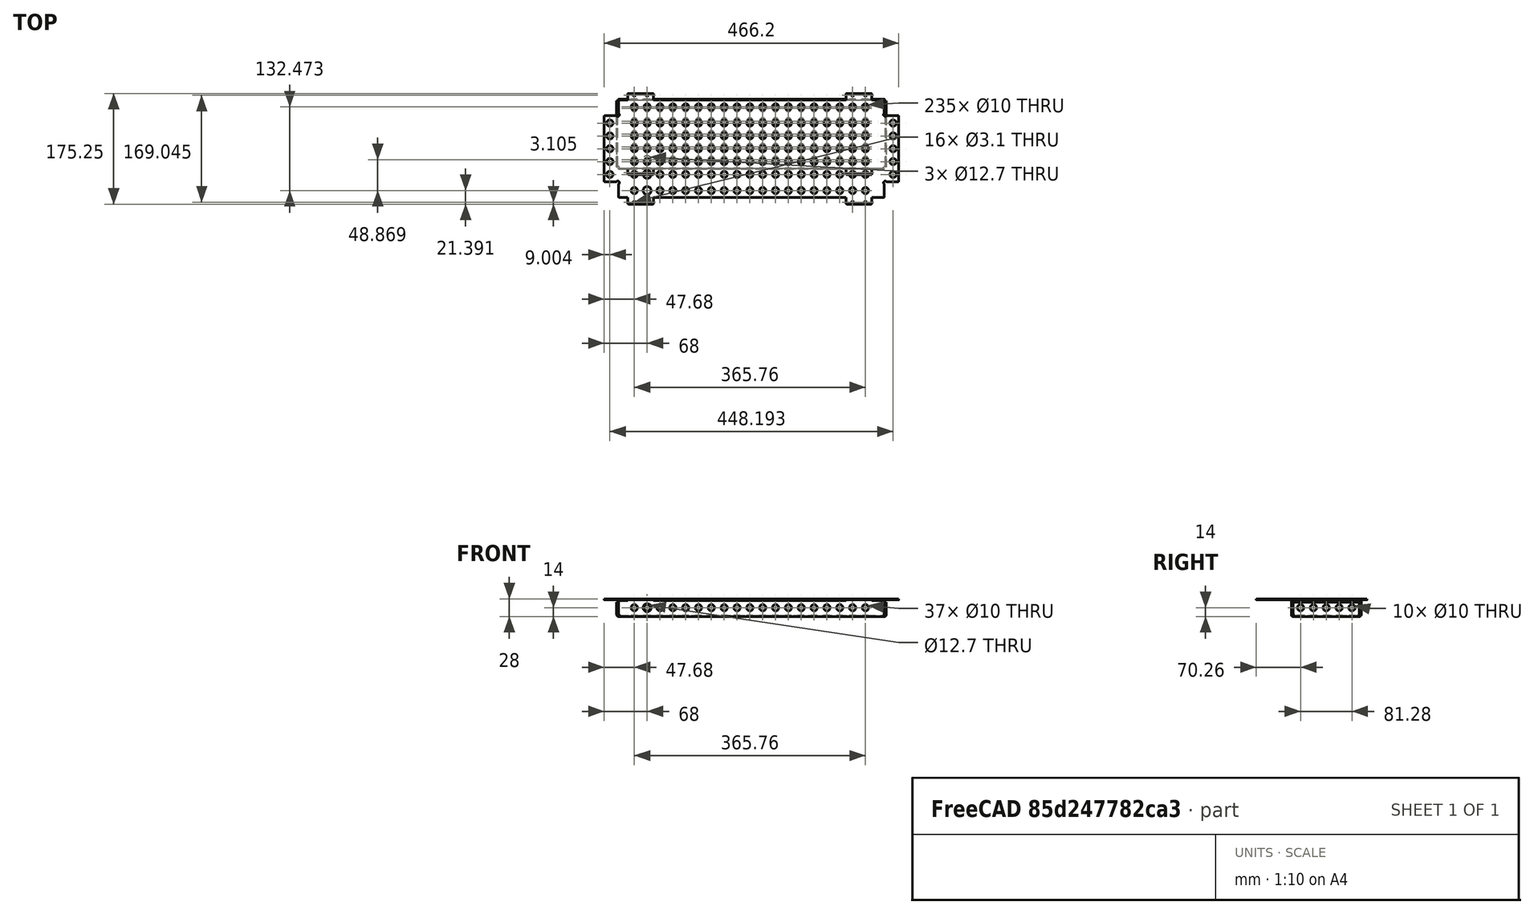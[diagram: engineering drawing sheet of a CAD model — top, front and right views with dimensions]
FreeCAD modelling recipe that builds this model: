
FCSTD DOCUMENT  (FreeCAD 0.21R33771 (Git))
Label: sheet_metal_rear_cover
License: All rights reserved
LicenseURL: http://en.wikipedia.org/wiki/All_rights_reserved
objects: TechDraw::DrawViewDimension×34, TechDraw::DrawViewBalloon×9, Sketcher::SketchObject×8, PartDesign::FeaturePython×7, PartDesign::Pocket×7, TechDraw::DrawViewAnnotation×6, PartDesign::LinearPattern×5, TechDraw::DrawSVGTemplate×5, TechDraw::DrawPage×5, PartDesign::MultiTransform×4, TechDraw::DrawViewPart×4, TechDraw::DrawProjGroupItem×4, PartDesign::Mirrored×2, Spreadsheet::Sheet×1, PartDesign::Plane×1, PartDesign::Fillet×1, PartDesign::Body×1, TechDraw::DrawViewSection×1, TechDraw::DrawProjGroup×1, Part::Feature×1
note: 108 computed .brp shape members not serialized (recipe doc carries the construction recipe); baked Part::Feature solids carry a one-line shape summary decoded from their .brp

FEATURE [PartDesign::FeaturePython] BaseShape  # WARN: FeaturePython — macro-defined, semantics opaque (R4)
  fillGaps = true
  flangeWidth = 5
  height = 25
  length = 420.42
  radius = 1.5
  shapeType = 1
  thickness = 1.5
  width = 110.7
  expr: height = Spreadsheet.h_cover - Spreadsheet.r_bending - Spreadsheet.t_cover
  expr: length = Spreadsheet.l_pcb - 2 * (Spreadsheet.r_bending + Spreadsheet.t_cover)
  expr: radius = Spreadsheet.r_bending
  expr: thickness = Spreadsheet.t_cover
  expr: width = Spreadsheet.h_pcb - 2 * Spreadsheet.d_ears + 2 * Spreadsheet.r_bending
FEATURE [PartDesign::FeaturePython] Bend  # WARN: FeaturePython — macro-defined, semantics opaque (R4)
  AutoMiter = true
  BaseFeature = -> BaseShape
  BendType = 0
  LengthList = [7.5]
  LengthSpec = 0
  ReliefFactor = 0.7
  UseReliefFactor = false
  angle = 90
  baseObject = -> BaseShape [Face21,Face3]
  bendAList = [90]
  extend1 = 0
  extend2 = 0
  gap1 = 0
  gap2 = 0
  invert = true
  kfactor = 0.5
  length = 7.5
  maxExtendDist = 5
  minGap = 0.2
  minReliefGap = 1
  miterangle1 = 0
  miterangle2 = 0
  offset = 0
  radius = 1.5
  reliefType = 0
  reliefd = 1
  reliefw = 0.8
  sketchflip = false
  sketchinvert = false
  unfold = false
  expr: length = Spreadsheet.d_ears - (Spreadsheet.t_cover + Spreadsheet.r_bending)
  expr: radius = Spreadsheet.r_bending
FEATURE [PartDesign::FeaturePython] Bend002  label="Bend001"  # WARN: FeaturePython — macro-defined, semantics opaque (R4)
  AutoMiter = true
  BaseFeature = -> Bend
  BendType = 0
  LengthList = [20]
  LengthSpec = 0
  ReliefFactor = 0.7
  UseReliefFactor = false
  angle = 90
  baseObject = -> Bend [Face17,Face22]
  bendAList = [90]
  extend1 = 0
  extend2 = 0
  gap1 = 0
  gap2 = 0
  invert = false
  kfactor = 0.5
  length = 20
  maxExtendDist = 5
  minGap = 0.2
  minReliefGap = 1
  miterangle1 = 0
  miterangle2 = 0
  offset = 0
  radius = 1.5
  reliefType = 0
  reliefd = 1
  reliefw = 0.8
  sketchflip = false
  sketchinvert = false
  unfold = false
  expr: radius = Spreadsheet.r_bending
FEATURE [Spreadsheet::Sheet] Spreadsheet
  cells = A1='y_first_screw; B1(y_first_screw)==3.1 mm; A2='x_first_screw; B2(x_first_screw)==7.47 mm; A3='dia_venting_hole; B3(dia_venting_hole)==10 mm; A4='h_pcb; B4(h_pcb)==128.7 mm; A5='h_cover; B5(h_cover)==28 mm; A6='t_cover; B6(t_cover)==1.5 mm; A7='d_ears; B7(d_ears)==10.5 mm; A8='d_venting_hole; B8(d_venting_hole)==4 * 5.08 mm; A9='l_pcb; B9(l_pcb)==426.42 mm; A10='d_grommet; B10(d_grommet)==25.4 mm / 2; A11='d_screws; B11(d_screws)==20 * 5.08 mm; A12='d_mounting_holes; B12(d_mounting_holes)==4 * 5.08 mm; A13='r_bending; B13(r_bending)==1.5 mm; A14='courtyard_edge; B14(courtyard_edge)==3 * t_cover; A15='dia_mounting_hole; B15(dia_mounting_hole)==3.1 mm; C15='Loose fit
FEATURE [Sketcher::SketchObject] Sketch001
  FullyConstrained = true
  MapMode = 5
  Placement = pos=(0,3.1e-15,28) rot=(0,0,1;0rad)
  expr: Constraints[0] = Spreadsheet.dia_mounting_hole
  expr: Constraints[1] = Spreadsheet.x_first_screw - Spreadsheet.r_bending - Spreadsheet.t_cover + Spreadsheet.d_mounting_holes
  expr: Constraints[2] = Spreadsheet.d_ears + Spreadsheet.r_bending - Spreadsheet.y_first_screw
  sketch-geometry (1):
    g0: Circle CenterX=24.79 CenterY=-8.9 CenterZ=0 NormalX=0 NormalY=0 NormalZ=1 AngleXU=0 Radius=1.55
  constraints (3):
    c: Diameter(g0) = 3.1
    c: DistanceX(g-1,g0) = 24.79
    c: DistanceY(g0,g-1) = 8.9
FEATURE [PartDesign::Pocket] Pocket001
  BaseFeature = -> Bend002
  Direction = (0,0,-1)
  Length = 1.6
  Length2 = 5
  Profile = -> Sketch001
  ReferenceAxis = -> Sketch001 [N_Axis]
  Type = 2
FEATURE [Sketcher::SketchObject] Sketch002
  ExternalGeometry = -> [Pocket001]
  FullyConstrained = true
  MapMode = 5
  Placement = pos=(0,-3,0) rot=(1,0,0;1.5708rad)
  Support = -> [Pocket001]
  expr: .Constraints.x_venting_hole = Spreadsheet.x_first_screw - Spreadsheet.r_bending - Spreadsheet.t_cover + Spreadsheet.d_venting_hole
  expr: .Constraints.y_venting_hole = (Spreadsheet.h_cover - 2 * Spreadsheet.t_cover - 2 * Spreadsheet.r_bending - 2 * Spreadsheet.courtyard_edge - Spreadsheet.dia_venting_hole) % Spreadsheet.d_venting_hole / 2 + Spreadsheet.t_cover + Spreadsheet.r_bending + Spreadsheet.courtyard_edge + Spreadsheet.dia_venting_hole / 2
  expr: Constraints[0] = Spreadsheet.dia_venting_hole
  sketch-geometry (1):
    g0: Circle CenterX=24.79 CenterY=14 CenterZ=0 NormalX=0 NormalY=0 NormalZ=1 AngleXU=0 Radius=5
  constraints (3):
    c: Diameter(g0) = 10
    c: DistanceY(g-1,g0) = 14  'y_venting_hole'
    c: DistanceX(g-1,g0) = 24.79  'x_venting_hole'
FEATURE [PartDesign::Pocket] Pocket002
  BaseFeature = -> Pocket001
  Direction = (0,1,-2e-16)
  Length = 1.6
  Length2 = 5
  Profile = -> Sketch002
  ReferenceAxis = -> Sketch002 [N_Axis]
  Type = 1
FEATURE [Sketcher::SketchObject] Sketch003
  FullyConstrained = true
  MapMode = 5
  Placement = pos=(0,0,0) rot=(1,0,0;3.14159rad)
  Support = -> [Pocket002]
  expr: .Constraints.x_venting_hole = Sketch002.Constraints.x_venting_hole
  expr: .Constraints.y_venting_hole = (Spreadsheet.h_pcb - trunc((Spreadsheet.h_pcb - 2 * (Spreadsheet.d_ears + Spreadsheet.r_bending + Spreadsheet.courtyard_edge) - Spreadsheet.dia_venting_hole) / Spreadsheet.d_venting_hole) * Spreadsheet.d_venting_hole) / 2 - Spreadsheet.d_ears - Spreadsheet.r_bending
  expr: Constraints[0] = Spreadsheet.dia_venting_hole
  sketch-geometry (1):
    g0: Circle CenterX=24.79 CenterY=-11.71 CenterZ=0 NormalX=0 NormalY=0 NormalZ=1 AngleXU=0 Radius=5
  constraints (3):
    c: Diameter(g0) = 10
    c: DistanceX(g-1,g0) = 24.79  'x_venting_hole'
    c: DistanceY(g0,g-1) = 11.71  'y_venting_hole'
FEATURE [PartDesign::Pocket] Pocket003
  BaseFeature = -> Pocket002
  Direction = (0,0,1)
  Length = 1.6
  Length2 = 5
  Profile = -> Sketch003
  ReferenceAxis = -> Sketch003 [N_Axis]
  Type = 0
FEATURE [Sketcher::SketchObject] Sketch004
  FullyConstrained = true
  MapMode = 5
  Placement = pos=(0,0,0) rot=(1,0,0;3.14159rad)
  Support = -> [Pocket003]
  expr: .Constraints.x_cable_feedthrough = Sketch003.Constraints.x_venting_hole + Spreadsheet.d_venting_hole
  expr: .Constraints.y_cable_feedthrough = Sketch003.Constraints.y_venting_hole
  expr: Constraints[0] = Spreadsheet.d_grommet
  sketch-geometry (1):
    g0: Circle CenterX=45.11 CenterY=-11.71 CenterZ=0 NormalX=0 NormalY=0 NormalZ=1 AngleXU=0 Radius=6.35
  constraints (3):
    c: Diameter(g0) = 12.7
    c: DistanceX(g-1,g0) = 45.11  'x_cable_feedthrough'
    c: DistanceY(g0,g-1) = 11.71  'y_cable_feedthrough'
FEATURE [PartDesign::LinearPattern] LinearPattern001
  Direction = -> Sketch002 [H_Axis]
  Length = 365.76
  Occurrences = 19
  expr: Length = trunc((Spreadsheet.l_pcb - (Sketch002.Constraints.x_venting_hole + 2 * Spreadsheet.r_bending + 2 * Spreadsheet.t_cover + Spreadsheet.courtyard_edge)) / Spreadsheet.d_venting_hole - 1) * Spreadsheet.d_venting_hole
  expr: Occurrences = trunc((Spreadsheet.l_pcb - (Sketch002.Constraints.x_venting_hole + Spreadsheet.r_bending + Spreadsheet.t_cover + Spreadsheet.courtyard_edge)) / Spreadsheet.d_venting_hole)
FEATURE [PartDesign::LinearPattern] LinearPattern002
  Direction = -> Sketch003 [V_Axis]
  Length = 81.28
  Occurrences = 5
  Reversed = true
  expr: Length = trunc((Spreadsheet.h_pcb - 2 * (Spreadsheet.d_ears + Spreadsheet.r_bending + Spreadsheet.courtyard_edge)) / Spreadsheet.d_venting_hole) * Spreadsheet.d_venting_hole
  expr: Occurrences = trunc((Spreadsheet.h_pcb - 2 * (Spreadsheet.d_ears + Spreadsheet.r_bending + Spreadsheet.courtyard_edge)) / Spreadsheet.d_venting_hole) + 1
FEATURE [PartDesign::LinearPattern] LinearPattern003
  Direction = -> Sketch003 [H_Axis]
  Length = 365.76
  Occurrences = 19
  expr: Length = trunc((Spreadsheet.l_pcb - (Sketch002.Constraints.x_venting_hole + 2 * Spreadsheet.r_bending + 2 * Spreadsheet.t_cover + Spreadsheet.courtyard_edge)) / Spreadsheet.d_venting_hole - 1) * Spreadsheet.d_venting_hole
  expr: Occurrences = trunc((Spreadsheet.l_pcb - (Sketch002.Constraints.x_venting_hole + 2 * Spreadsheet.r_bending + 2 * Spreadsheet.t_cover + Spreadsheet.courtyard_edge)) / Spreadsheet.d_venting_hole)
FEATURE [Sketcher::SketchObject] Sketch009
  FullyConstrained = true
  MapMode = 5
  Placement = pos=(-3,0,0) rot=(0.57735,-0.57735,-0.57735;2.0944rad)
  Support = -> [Pocket003]
  expr: Constraints[0] = Spreadsheet.dia_venting_hole
  expr: Constraints[1] = Sketch002.Constraints.y_venting_hole
  expr: Constraints[2] = Sketch003.Constraints.y_venting_hole
  sketch-geometry (1):
    g0: Circle CenterX=-11.71 CenterY=14 CenterZ=0 NormalX=0 NormalY=0 NormalZ=1 AngleXU=0 Radius=5
  constraints (3):
    c: Diameter(g0) = 10
    c: DistanceY(g-1,g0) = 14
    c: DistanceX(g0,g-1) = 11.71
FEATURE [PartDesign::Pocket] Pocket006
  BaseFeature = -> Pocket003
  Direction = (1,0,0)
  Length = 5
  Length2 = 5
  Profile = -> Sketch009
  ReferenceAxis = -> Sketch009 [N_Axis]
  Type = 1
FEATURE [PartDesign::Pocket] Pocket004
  BaseFeature = -> Pocket006
  Direction = (0,0,1)
  Length = 1.5
  Length2 = 5
  Profile = -> Sketch004
  ReferenceAxis = -> Sketch004 [N_Axis]
  Type = 0
FEATURE [Sketcher::SketchObject] Sketch005
  FullyConstrained = true
  MapMode = 5
  Placement = pos=(0,-3,0) rot=(1,0,0;1.5708rad)
  Support = -> [Pocket004]
  expr: .Constraints.x_cable_feedthrough = Sketch004.Constraints.x_cable_feedthrough
  expr: .Constraints.y_cable_feedthrough = Sketch002.Constraints.y_venting_hole
  expr: Constraints[0] = Spreadsheet.d_grommet
  sketch-geometry (1):
    g0: Circle CenterX=45.11 CenterY=14 CenterZ=0 NormalX=0 NormalY=0 NormalZ=1 AngleXU=0 Radius=6.35
  constraints (3):
    c: Diameter(g0) = 12.7
    c: DistanceY(g-1,g0) = 14  'y_cable_feedthrough'
    c: DistanceX(g-1,g0) = 45.11  'x_cable_feedthrough'
FEATURE [PartDesign::Pocket] Pocket005
  BaseFeature = -> Pocket004
  Direction = (0,1,-2e-16)
  Length = 1.6
  Length2 = 5
  Profile = -> Sketch005
  ReferenceAxis = -> Sketch005 [N_Axis]
  Type = 0
FEATURE [PartDesign::LinearPattern] LinearPattern005
  Direction = -> Sketch009 [H_Axis]
  Length = 81.28
  Occurrences = 5
  Reversed = true
  expr: Length = trunc((Spreadsheet.h_pcb - 2 * (Spreadsheet.d_ears + Spreadsheet.r_bending + Spreadsheet.courtyard_edge)) / Spreadsheet.d_venting_hole) * Spreadsheet.d_venting_hole
  expr: Occurrences = trunc((Spreadsheet.h_pcb - 2 * (Spreadsheet.d_ears + Spreadsheet.r_bending + Spreadsheet.courtyard_edge)) / Spreadsheet.d_venting_hole) + 1
FEATURE [PartDesign::Plane] DatumPlane
  AttachmentOffset = pos=(0,0,52.35) rot=(0,0,1;0rad)
  Length = 60
  MapMode = 5
  Placement = pos=(0,52.35,1.16e-14) rot=(0,0.707107,0.707107;3.14159rad)
  ResizeMode = 0
  Support = -> [XZ_Plane]
  Width = 60
  expr: .AttachmentOffset.Base.z = (Spreadsheet.h_pcb - 2 * Spreadsheet.d_ears - 2 * Spreadsheet.r_bending) / 2
FEATURE [PartDesign::MultiTransform] MultiTransform
  BaseFeature = -> Pocket005
  Originals = -> [Pocket002]
  Transformations = -> [LinearPattern001]
FEATURE [PartDesign::MultiTransform] MultiTransform001
  BaseFeature = -> MultiTransform
  Originals = -> [Pocket003]
  Transformations = -> [LinearPattern002,LinearPattern003]
FEATURE [PartDesign::MultiTransform] MultiTransform002
  BaseFeature = -> MultiTransform001
  Originals = -> [Pocket006]
  Transformations = -> [LinearPattern005]
FEATURE [Sketcher::SketchObject] Sketch010
  FullyConstrained = true
  MapMode = 5
  Placement = pos=(0,0,28) rot=(0,0,1;0rad)
  Support = -> [MultiTransform002]
  expr: Constraints[10] = Spreadsheet.d_ears
  expr: Constraints[11] = Spreadsheet.x_first_screw - (Spreadsheet.r_bending + Spreadsheet.t_cover) + 0.5 * Spreadsheet.d_venting_hole
  expr: Constraints[22] = 2 * Spreadsheet.d_mounting_holes
  expr: Constraints[33] = 2 * Spreadsheet.d_venting_hole
  expr: Constraints[34] = Spreadsheet.l_pcb - 2 * (Spreadsheet.t_cover + Spreadsheet.r_bending)
  expr: Constraints[35] = trunc((Spreadsheet.l_pcb - Spreadsheet.x_first_screw - 2 * Spreadsheet.t_cover - 2 * Spreadsheet.r_bending) / Spreadsheet.d_mounting_holes - 1) * Spreadsheet.d_mounting_holes + Spreadsheet.x_first_screw - Spreadsheet.r_bending - Spreadsheet.t_cover + 0.5 * Spreadsheet.d_venting_hole
  expr: Constraints[9] = Spreadsheet.t_cover
  sketch-geometry (12):
    g0: LineSegment StartX=0 StartY=-1.5 StartZ=0 EndX=14.63 EndY=-1.5 EndZ=0
    g1: LineSegment StartX=14.63 StartY=-1.5 StartZ=0 EndX=14.63 EndY=-12 EndZ=0
    g2: LineSegment StartX=14.63 StartY=-12 StartZ=0 EndX=0 EndY=-12 EndZ=0
    g3: LineSegment StartX=0 StartY=-12 StartZ=0 EndX=0 EndY=-1.5 EndZ=0
    g4: LineSegment StartX=55.27 StartY=-1.5 StartZ=0 EndX=360.07 EndY=-1.5 EndZ=0
    g5: LineSegment StartX=360.07 StartY=-1.5 StartZ=0 EndX=360.07 EndY=-12 EndZ=0
    g6: LineSegment StartX=360.07 StartY=-12 StartZ=0 EndX=55.27 EndY=-12 EndZ=0
    g7: LineSegment StartX=55.27 StartY=-12 StartZ=0 EndX=55.27 EndY=-1.5 EndZ=0
    g8: LineSegment StartX=400.71 StartY=-1.5 StartZ=0 EndX=420.42 EndY=-1.5 EndZ=0
    g9: LineSegment StartX=420.42 StartY=-1.5 StartZ=0 EndX=420.42 EndY=-12 EndZ=0
    g10: LineSegment StartX=420.42 StartY=-12 StartZ=0 EndX=400.71 EndY=-12 EndZ=0
    g11: LineSegment StartX=400.71 StartY=-12 StartZ=0 EndX=400.71 EndY=-1.5 EndZ=0
  constraints (36):
    c: Coincident(g0,g1)
    c: Coincident(g1,g2)
    c: Coincident(g2,g3)
    c: Coincident(g3,g0)
    c: Horizontal(g0)
    c: Horizontal(g2)
    c: Vertical(g1)
    c: Vertical(g3)
    c: PointOnObject(g0,g-2)
    c: DistanceY(g0,g-1) = 1.5
    c: DistanceY(g3,g3) = 10.5
    c: DistanceX(g2,g2) = 14.63
    c: Coincident(g4,g5)
    c: Coincident(g5,g6)
    c: Coincident(g6,g7)
    c: Coincident(g7,g4)
    c: Horizontal(g4)
    c: Horizontal(g6)
    c: Vertical(g5)
    c: Vertical(g7)
    c: Horizontal(g1,g6)
    c: Horizontal(g4,g0)
    c: DistanceX(g1,g6) = 40.64
    c: Coincident(g8,g9)
    c: Coincident(g9,g10)
    c: Coincident(g10,g11)
    c: Coincident(g11,g8)
    c: Horizontal(g8)
    c: Horizontal(g10)
    c: Vertical(g9)
    c: Vertical(g11)
    c: Horizontal(g8,g4)
    c: Horizontal(g10,g5)
    c: DistanceX(g5,g10) = 40.64
    c: DistanceX(g-1,g9) = 420.42
    c: DistanceX(g-1,g10) = 400.71
FEATURE [PartDesign::LinearPattern] LinearPattern
  Direction = -> Sketch010 [H_Axis]
  Length = 406.4
  Occurrences = 21
  expr: Length = trunc((Spreadsheet.l_pcb - (Spreadsheet.x_first_screw + Spreadsheet.r_bending + Spreadsheet.t_cover)) / Spreadsheet.d_mounting_holes) * Spreadsheet.d_mounting_holes
  expr: Occurrences = trunc((Spreadsheet.l_pcb - (Spreadsheet.x_first_screw + Spreadsheet.r_bending + Spreadsheet.t_cover)) / Spreadsheet.d_mounting_holes) + 1
FEATURE [PartDesign::Mirrored] Mirrored
  MirrorPlane = -> DatumPlane
FEATURE [PartDesign::MultiTransform] MultiTransform003
  BaseFeature = -> MultiTransform002
  Originals = -> [Pocket001]
  Transformations = -> [LinearPattern,Mirrored]
FEATURE [PartDesign::Pocket] Pocket007
  BaseFeature = -> MultiTransform003
  Direction = (0,0,-1)
  Length = 3
  Length2 = 5
  Profile = -> Sketch010
  ReferenceAxis = -> Sketch010 [N_Axis]
  Type = 0
  expr: Length = Spreadsheet.r_bending + Spreadsheet.t_cover
FEATURE [PartDesign::Mirrored] Mirrored001
  BaseFeature = -> Pocket007
  MirrorPlane = -> DatumPlane
  Originals = -> [Pocket007]
FEATURE [PartDesign::Fillet] Fillet
  Base = -> Mirrored001 [Edge562,Edge558,Edge476,Edge516,Edge515,Edge522,Edge582,Edge589,Edge591,Edge580,Edge403,Edge8,Edge2,Edge239,Edge513,Edge567]
  BaseFeature = -> Mirrored001
  Radius = 1
  SupportTransform = false
  UseAllEdges = false
FEATURE [PartDesign::FeaturePython] CornerRelief  # WARN: FeaturePython — macro-defined, semantics opaque (R4)
  BaseFeature = -> Fillet
  ReliefSketch = 0
  Size = 3
  SizeRatio = 1.5
  XOffset = 0
  YOffset = 0
  baseObject = -> Fillet [Edge45,Edge46]
  kfactor = 0.45
FEATURE [PartDesign::FeaturePython] CornerRelief001  # WARN: FeaturePython — macro-defined, semantics opaque (R4)
  BaseFeature = -> CornerRelief
  ReliefSketch = 0
  Size = 3
  SizeRatio = 1.5
  XOffset = 0
  YOffset = 0
  baseObject = -> CornerRelief [Edge46,Edge45]
  kfactor = 0.45
FEATURE [TechDraw::DrawSVGTemplate] Template
  EditableTexts = AUTHOR_NAME=P. Baus/J. Götzinger; DN=DN; DRAWING_TITLE=Backplane cover; FC-DATE=07/01/2034; FC-REV=1.0.0; FC-SC=1:2; FC-SH=1 / 5; FC-SI=A4; FreeCAD_DRAWING=TUD, Institut für Angewandte Physik, APQ; PN=PN; SI-1=Email: <email>; SI-3=Material: Stainless steel 430
  Height = 210
  Orientation = 1
  Template = <path>
  Width = 297
FEATURE [TechDraw::DrawSVGTemplate] Template001
  EditableTexts = AUTHOR_NAME=P. Baus/J. Götzinger; DN=DN; DRAWING_TITLE=Backplane cover; FC-DATE=07/01/2024; FC-REV=1.0.0; FC-SC=1:4; FC-SH=2 / 5; FC-SI=A4; FreeCAD_DRAWING=TUD, Institut für Angewandte Physik, APQ; PN=PN; SI-1=Email: <email>; SI-3=Material: Stainless steel 430
  Height = 210
  Orientation = 1
  Template = <path>
  Width = 297
FEATURE [TechDraw::DrawViewAnnotation] Annotation
  Font = osifont
  LineSpace = 100
  LockPosition = false
  MaxWidth = -1
  Rotation = 0
  Scale = 0.25
  ScaleType = 0
  Text = Bending sequence: Bend the central part first to maintain | tight tolerances in the horizontal direction.
  TextSize = 2.5
  TextStyle = 0
  X = 172.812
  Y = 74.2756
FEATURE [TechDraw::DrawSVGTemplate] Template002
  EditableTexts = AUTHOR_NAME=P. Baus/J. Götzinger; DN=DN; DRAWING_TITLE=Backplane cover; FC-DATE=07/01/2024; FC-REV=1.0.0; FC-SC=1:2; FC-SH=3 / 5; FC-SI=A4; FreeCAD_DRAWING=TUD, Institut für Angewandte Physik, APQ; PN=PN; SI-1=Email: <email>; SI-3=Material: Stainless steel 430
  Height = 210
  Orientation = 1
  Template = <path>
  Width = 297
FEATURE [TechDraw::DrawViewAnnotation] Annotation001
  Font = osifont
  LineSpace = 100
  LockPosition = false
  MaxWidth = -1
  Rotation = 0
  Scale = 0.5
  ScaleType = 0
  Text = 1: Mounting hole x8
  TextSize = 2.5
  TextStyle = 0
  X = 26.501
  Y = 183.431
FEATURE [TechDraw::DrawViewAnnotation] Annotation002
  Font = osifont
  LineSpace = 100
  LockPosition = false
  MaxWidth = -1
  Rotation = 0
  Scale = 0.5
  ScaleType = 0
  Text = The 8 mounting holes must be CNC | machined after bending to meet the | location tolerances.
  TextSize = 2.5
  TextStyle = 0
  X = 155.836
  Y = 177.813
FEATURE [TechDraw::DrawViewAnnotation] Annotation003
  Font = osifont
  LineSpace = 100
  LockPosition = false
  MaxWidth = -1
  Rotation = 0
  Scale = 0.25
  ScaleType = 0
  Text = Bottom
  TextSize = 2.5
  TextStyle = 0
  X = 214.052
  Y = 152.612
FEATURE [TechDraw::DrawViewAnnotation] Annotation004
  Font = osifont
  LineSpace = 100
  LockPosition = false
  MaxWidth = -1
  Rotation = 0
  Scale = 0.25
  ScaleType = 0
  Text = Top
  TextSize = 2.5
  TextStyle = 0
  X = 274.545
  Y = 118.11
FEATURE [PartDesign::FeaturePython] CornerRelief002  # WARN: FeaturePython — macro-defined, semantics opaque (R4)
  BaseFeature = -> CornerRelief001
  ReliefSketch = 0
  Size = 3
  SizeRatio = 1.5
  XOffset = 0
  YOffset = 0
  baseObject = -> CornerRelief001 [Edge47,Edge33]
  kfactor = 0.5
FEATURE [PartDesign::FeaturePython] CornerRelief003  # WARN: FeaturePython — macro-defined, semantics opaque (R4)
  BaseFeature = -> CornerRelief002
  ReliefSketch = 0
  Size = 3
  SizeRatio = 1.5
  XOffset = 0
  YOffset = 0
  baseObject = -> CornerRelief002 [Edge33,Edge51]
  kfactor = 0.5
FEATURE [PartDesign::Body] Body  label="Cover"
  Group = -> [BaseShape,Bend,Bend002,Sketch001,Pocket001,Sketch002,Pocket002,Sketch003,Pocket003,Pocket006,Sketch009,Sketch004,Pocket004,Sketch005,Pocket005,MultiTransform,LinearPattern001,MultiTransform001,MultiTransform002,DatumPlane,LinearPattern002,LinearPattern003,LinearPattern005,Sketch010,MultiTransform003,Pocket007,Mirrored001,Fillet,CornerRelief,CornerRelief001,LinearPattern,Mirrored,CornerRelief002,+1 more]
  Origin = -> Origin
  Tip = -> CornerRelief003
FEATURE [TechDraw::DrawViewPart] View
  CoarseView = false
  Direction = (-0.57735,-0.57735,-0.57735)
  Focus = 100
  HardHidden = false
  IsoCount = 0
  IsoHidden = false
  IsoVisible = false
  LockPosition = false
  Perspective = false
  Rotation = 0
  Scale = 0.5
  ScaleType = 0
  ScrubCount = 0
  SeamHidden = false
  SeamVisible = true
  SmoothHidden = false
  SmoothVisible = true
  Source = -> [Body]
  X = 148.063
  XDirection = (-0.707107,0.707106,5.7735e-07)
  Y = 121.615
FEATURE [TechDraw::DrawPage] Page
  KeepUpdated = true
  NextBalloonIndex = 1
  ProjectionType = 0
  Scale = 0.5
  Template = -> Template
  Views = -> [View]
FEATURE [TechDraw::DrawProjGroupItem] ProjItem  label="Bottom"
  Caption = Bottom
  CoarseView = false
  Direction = (0,0,1)
  Focus = 100
  HardHidden = false
  IsoCount = 0
  IsoHidden = false
  IsoVisible = false
  LockPosition = true
  Perspective = false
  Rotation = 0
  RotationVector = (0,-1,0)
  Scale = 0.25
  ScaleType = 2
  ScrubCount = 0
  SeamHidden = false
  SeamVisible = true
  SmoothHidden = false
  SmoothVisible = true
  Source = -> [Body]
  Type = 0
  X = 0
  XDirection = (0,-1,0)
  Y = 0
FEATURE [TechDraw::DrawViewDimension] Dimension001
  AngleOverride = false
  Arbitrary = false
  ArbitraryTolerances = false
  EqualTolerance = true
  ExtensionAngle = 0
  FormatSpec = %.2w
  FormatSpecOverTolerance = %+.2w
  FormatSpecUnderTolerance = %+.2w
  Inverted = false
  LineAngle = 0
  LockPosition = false
  MeasureType = 1
  OverTolerance = 0
  References2D = -> [ProjItem]
  Rotation = 0
  Scale = 0.25
  ScaleType = 0
  TheoreticalExact = false
  Type = 1
  UnderTolerance = 0
  X = -1.09639
  Y = 69.5073
FEATURE [TechDraw::DrawViewSection] SectionView  label="Section A - A"
  BaseView = -> ProjItem
  Caption = Section A - A (1:1)
  CoarseView = false
  CutSurfaceDisplay = 2
  Direction = (1,-1e-16,0)
  FileGeomPattern = <path>
  FileHatchPattern = <path>
  Focus = 100
  FuseBeforeCut = false
  HardHidden = false
  HatchOffset = (0,0,0)
  HatchRotation = 0
  HatchScale = 1
  IsoCount = 0
  IsoHidden = false
  IsoVisible = false
  LockPosition = false
  NameGeomPattern = Diamond
  Perspective = false
  Rotation = 0
  ScaleType = 2
  ScrubCount = 0
  SeamHidden = false
  SeamVisible = true
  SectionDirection = 4
  SectionNormal = (1,-1e-16,0)
  SectionOrigin = (34.95,52.35,14)
  SectionSymbol = A
  SmoothHidden = false
  SmoothVisible = true
  Source = -> [Body]
  TrimAfterCut = false
  X = 214.919
  XDirection = (-1e-16,-1,0)
  Y = 134.5
  expr: .SectionOrigin.x = Spreadsheet.x_first_screw - Spreadsheet.r_bending - Spreadsheet.t_cover + 1.5 * Spreadsheet.d_mounting_holes
FEATURE [TechDraw::DrawViewDimension] Dimension002
  AngleOverride = false
  Arbitrary = false
  ArbitraryTolerances = false
  EqualTolerance = true
  ExtensionAngle = 0
  FormatSpec = %.2w
  FormatSpecOverTolerance = %+.2w
  FormatSpecUnderTolerance = %+.2w
  Inverted = false
  LineAngle = 0
  LockPosition = false
  MeasureType = 1
  OverTolerance = 1
  References2D = -> [SectionView]
  Rotation = 0
  Scale = 0.25
  ScaleType = 0
  TheoreticalExact = false
  Type = 2
  UnderTolerance = -1
  X = -86.2598
  Y = 0.959543
FEATURE [TechDraw::DrawViewDimension] Dimension003
  AngleOverride = false
  Arbitrary = false
  ArbitraryTolerances = false
  EqualTolerance = true
  ExtensionAngle = 0
  FormatSpec = %.2w
  FormatSpecOverTolerance = %+.2w
  FormatSpecUnderTolerance = %+.2w
  Inverted = false
  LineAngle = 0
  LockPosition = false
  MeasureType = 1
  OverTolerance = 0.5
  References2D = -> [SectionView]
  Rotation = 0
  Scale = 0.25
  ScaleType = 0
  TheoreticalExact = false
  Type = 1
  UnderTolerance = -0.5
  X = -2.59902
  Y = 38.9474
FEATURE [TechDraw::DrawViewDimension] Dimension004
  AngleOverride = false
  Arbitrary = false
  ArbitraryTolerances = false
  EqualTolerance = true
  ExtensionAngle = 0
  FormatSpec = %.2w
  FormatSpecOverTolerance = %+.2w
  FormatSpecUnderTolerance = %+.2w
  Inverted = false
  LineAngle = 0
  LockPosition = false
  MeasureType = 1
  OverTolerance = 0.25
  References2D = -> [SectionView]
  Rotation = 0
  Scale = 0.25
  ScaleType = 0
  TheoreticalExact = false
  Type = 1
  UnderTolerance = -0.25
  X = 28.5957
  Y = -31.9761
FEATURE [TechDraw::DrawViewDimension] Dimension005
  AngleOverride = false
  Arbitrary = false
  ArbitraryTolerances = false
  EqualTolerance = true
  ExtensionAngle = 0
  FormatSpec = %.2w
  FormatSpecOverTolerance = %+.2w
  FormatSpecUnderTolerance = %+.2w
  Inverted = false
  LineAngle = 0
  LockPosition = false
  MeasureType = 1
  OverTolerance = 0.25
  References2D = -> [SectionView]
  Rotation = 0
  Scale = 0.25
  ScaleType = 0
  TheoreticalExact = false
  Type = 1
  UnderTolerance = -0.25
  X = -43.5059
  Y = -30.6082
FEATURE [TechDraw::DrawViewDimension] Dimension006
  AngleOverride = false
  Arbitrary = false
  ArbitraryTolerances = false
  EqualTolerance = true
  ExtensionAngle = 0
  FormatSpec = R%.2w
  FormatSpecOverTolerance = %+.2w
  FormatSpecUnderTolerance = %+.2w
  Inverted = false
  LineAngle = 0
  LockPosition = false
  MeasureType = 1
  OverTolerance = 0
  References2D = -> [SectionView]
  Rotation = 0
  Scale = 0.25
  ScaleType = 0
  TheoreticalExact = false
  Type = 4
  UnderTolerance = 0
  X = -73.5933
  Y = 3.69334
FEATURE [TechDraw::DrawViewDimension] Dimension007
  AngleOverride = false
  Arbitrary = false
  ArbitraryTolerances = false
  EqualTolerance = true
  ExtensionAngle = 0
  FormatSpec = %.2w
  FormatSpecOverTolerance = %+.2w
  FormatSpecUnderTolerance = %+.2w
  Inverted = false
  LineAngle = 0
  LockPosition = false
  MeasureType = 1
  OverTolerance = 0
  References2D = -> [SectionView]
  Rotation = 0
  Scale = 0.25
  ScaleType = 0
  TheoreticalExact = false
  Type = 2
  UnderTolerance = 0
  X = -73.577
  Y = -24.2095
FEATURE [TechDraw::DrawProjGroupItem] ProjItem001  label="Rear"
  Caption = Rear
  CoarseView = false
  Direction = (0,1,1e-16)
  Focus = 100
  HardHidden = false
  IsoCount = 0
  IsoHidden = false
  IsoVisible = false
  LockPosition = false
  Perspective = false
  Rotation = 0
  RotationVector = (1,0,0)
  ScaleType = 2
  ScrubCount = 0
  SeamHidden = false
  SeamVisible = true
  SmoothHidden = false
  SmoothVisible = true
  Source = -> [Body]
  Type = 1
  X = 34.5875
  XDirection = (0,-1e-16,1)
  Y = 0
FEATURE [TechDraw::DrawProjGroupItem] ProjItem002  label="Front"
  Caption = Front
  CoarseView = false
  Direction = (0,-1,1e-16)
  Focus = 100
  HardHidden = false
  IsoCount = 0
  IsoHidden = false
  IsoVisible = false
  LockPosition = false
  Perspective = false
  Rotation = 0
  RotationVector = (1,0,0)
  ScaleType = 2
  ScrubCount = 0
  SeamHidden = false
  SeamVisible = true
  SmoothHidden = false
  SmoothVisible = true
  Source = -> [Body]
  Type = 2
  X = -34.5875
  XDirection = (0,-1e-16,-1)
  Y = 0
FEATURE [TechDraw::DrawProjGroupItem] ProjItem003  label="Left"
  Caption = Left
  CoarseView = false
  Direction = (1,0,0)
  Focus = 100
  HardHidden = false
  IsoCount = 0
  IsoHidden = false
  IsoVisible = false
  LockPosition = false
  Perspective = false
  Rotation = 0
  RotationVector = (1,0,0)
  ScaleType = 2
  ScrubCount = 0
  SeamHidden = false
  SeamVisible = true
  SmoothHidden = false
  SmoothVisible = true
  Source = -> [Body]
  Type = 4
  X = 0
  XDirection = (0,-1,0)
  Y = -71.8025
FEATURE [TechDraw::DrawProjGroup] ProjGroup
  Anchor = -> ProjItem
  AutoDistribute = true
  LockPosition = false
  ProjectionType = 0
  Rotation = 0
  Scale = 0.25
  ScaleType = 0
  Source = -> [Body]
  Views = -> [ProjItem,ProjItem001,ProjItem002,ProjItem003]
  X = 64.0777
  Y = 119.042
  spacingX = 15
  spacingY = 15
FEATURE [TechDraw::DrawViewPart] View001
  Caption = Top View
  CoarseView = false
  Direction = (0,0,1)
  Focus = 100
  HardHidden = false
  IsoCount = 0
  IsoHidden = false
  IsoVisible = false
  LockPosition = false
  Perspective = false
  Rotation = 0
  Scale = 0.5
  ScaleType = 0
  ScrubCount = 0
  SeamHidden = false
  SeamVisible = true
  SmoothHidden = false
  SmoothVisible = true
  Source = -> [Body]
  X = 148.5
  XDirection = (1,0,0)
  Y = 105
FEATURE [TechDraw::DrawViewDimension] Dimension
  AngleOverride = false
  Arbitrary = false
  ArbitraryTolerances = false
  EqualTolerance = true
  ExtensionAngle = 0
  FormatSpec = %.2w
  FormatSpecOverTolerance = %+.2w
  FormatSpecUnderTolerance = %+.2w
  Inverted = false
  LineAngle = 0
  LockPosition = false
  MeasureType = 1
  OverTolerance = 0.1
  References2D = -> [View001]
  Rotation = 0
  Scale = 0.5
  ScaleType = 0
  TheoreticalExact = false
  Type = 1
  UnderTolerance = -0.1
  X = -109.46
  Y = 42.7519
FEATURE [TechDraw::DrawViewDimension] Dimension008
  AngleOverride = false
  Arbitrary = false
  ArbitraryTolerances = false
  EqualTolerance = true
  ExtensionAngle = 0
  FormatSpec = %.2w
  FormatSpecOverTolerance = %+.2w
  FormatSpecUnderTolerance = %+.2w
  Inverted = false
  LineAngle = 0
  LockPosition = false
  MeasureType = 1
  OverTolerance = 0.1
  References2D = -> [View001]
  Rotation = 0
  Scale = 0.5
  ScaleType = 0
  TheoreticalExact = false
  Type = 1
  UnderTolerance = -0.1
  X = -6.35
  Y = 47.4779
FEATURE [TechDraw::DrawViewDimension] Dimension009
  AngleOverride = false
  Arbitrary = false
  ArbitraryTolerances = false
  EqualTolerance = true
  ExtensionAngle = 0
  FormatSpec = %.2w
  FormatSpecOverTolerance = %+.2w
  FormatSpecUnderTolerance = %+.2w
  Inverted = false
  LineAngle = 0
  LockPosition = false
  MeasureType = 1
  OverTolerance = 0.1
  References2D = -> [View001]
  Rotation = 0
  Scale = 0.5
  ScaleType = 0
  TheoreticalExact = false
  Type = 1
  UnderTolerance = -0.1
  X = 1.20557
  Y = 53.7794
FEATURE [TechDraw::DrawViewDimension] Dimension010
  AngleOverride = false
  Arbitrary = false
  ArbitraryTolerances = false
  EqualTolerance = true
  ExtensionAngle = 0
  FormatSpec = %.2w
  FormatSpecOverTolerance = %+.2w
  FormatSpecUnderTolerance = %+.2w
  Inverted = false
  LineAngle = 0
  LockPosition = false
  MeasureType = 1
  OverTolerance = 0.1
  References2D = -> [View001]
  Rotation = 0
  Scale = 0.5
  ScaleType = 0
  TheoreticalExact = false
  Type = 2
  UnderTolerance = -0.1
  X = 118.601
  Y = 1.92515
FEATURE [TechDraw::DrawViewDimension] Dimension011
  AngleOverride = false
  Arbitrary = false
  ArbitraryTolerances = false
  EqualTolerance = true
  ExtensionAngle = 0
  FormatSpec = ⌀%.2w THRU
  FormatSpecOverTolerance = %+.2w
  FormatSpecUnderTolerance = %+.2w
  Inverted = false
  LineAngle = 0
  LockPosition = false
  MeasureType = 1
  OverTolerance = 0
  References2D = -> [View001]
  Rotation = 0
  Scale = 0.5
  ScaleType = 0
  TheoreticalExact = false
  Type = 5
  UnderTolerance = 0
  X = 108.7
  Y = -41.4095
FEATURE [TechDraw::DrawViewDimension] Dimension012
  AngleOverride = false
  Arbitrary = false
  ArbitraryTolerances = false
  EqualTolerance = true
  ExtensionAngle = 0
  FormatSpec = ⌀%.2w THRU
  FormatSpecOverTolerance = %+.2w
  FormatSpecUnderTolerance = %+.2w
  Inverted = false
  LineAngle = 0
  LockPosition = false
  MeasureType = 1
  OverTolerance = 0
  References2D = -> [View001]
  Rotation = 0
  Scale = 0.5
  ScaleType = 0
  TheoreticalExact = false
  Type = 5
  UnderTolerance = 0
  X = -16.6538
  Y = -45.4604
FEATURE [TechDraw::DrawViewDimension] Dimension013
  AngleOverride = false
  Arbitrary = false
  ArbitraryTolerances = false
  EqualTolerance = true
  ExtensionAngle = 0
  FormatSpec = ⌀%.2w THRU
  FormatSpecOverTolerance = %+.2w
  FormatSpecUnderTolerance = %+.2w
  Inverted = false
  LineAngle = 0
  LockPosition = false
  MeasureType = 1
  OverTolerance = 0
  References2D = -> [View001]
  Rotation = 0
  Scale = 0.5
  ScaleType = 0
  TheoreticalExact = false
  Type = 5
  UnderTolerance = 0
  X = -45.2353
  Y = -46.3606
FEATURE [TechDraw::DrawViewBalloon] Balloon
  BubbleShape = 0
  EndType = 0
  EndTypeScale = 1
  KinkLength = 5
  LockPosition = false
  OriginX = -186.97
  OriginY = -61.25
  Rotation = 0
  Scale = 0.5
  ScaleType = 0
  ShapeScale = 1
  SourceView = -> View001
  Text = 1
  TextWrapLen = -1
  X = -226.188
  Y = -98.2176
FEATURE [TechDraw::DrawViewDimension] Dimension014
  AngleOverride = false
  Arbitrary = false
  ArbitraryTolerances = false
  EqualTolerance = true
  ExtensionAngle = 0
  FormatSpec = %.2w
  FormatSpecOverTolerance = %+.2w
  FormatSpecUnderTolerance = %+.2w
  Inverted = false
  LineAngle = 0
  LockPosition = false
  MeasureType = 1
  OverTolerance = 0
  References2D = -> [View001]
  Rotation = 0
  Scale = 0.5
  ScaleType = 0
  TheoreticalExact = false
  Type = 2
  UnderTolerance = 0
  X = -126.694
  Y = -14.4401
FEATURE [TechDraw::DrawViewDimension] Dimension015
  AngleOverride = false
  Arbitrary = false
  ArbitraryTolerances = false
  EqualTolerance = true
  ExtensionAngle = 0
  FormatSpec = %.2w
  FormatSpecOverTolerance = %+.2w
  FormatSpecUnderTolerance = %+.2w
  Inverted = false
  LineAngle = 0
  LockPosition = false
  MeasureType = 1
  OverTolerance = 0
  References2D = -> [View001]
  Rotation = 0
  Scale = 0.5
  ScaleType = 0
  TheoreticalExact = false
  Type = 1
  UnderTolerance = 0
  X = -87.4049
  Y = -46.0772
FEATURE [TechDraw::DrawPage] Page002
  KeepUpdated = true
  NextBalloonIndex = 2
  ProjectionType = 0
  Scale = 0.5
  Template = -> Template002
  Views = -> [Annotation001,Annotation002,View001,Dimension,Dimension008,Dimension009,Dimension010,Dimension011,Dimension012,Dimension013,Balloon,Dimension014,Dimension015]
FEATURE [TechDraw::DrawViewDimension] Dimension016
  AngleOverride = false
  Arbitrary = false
  ArbitraryTolerances = false
  EqualTolerance = true
  ExtensionAngle = 0
  FormatSpec = %.2w
  FormatSpecOverTolerance = %+.2w
  FormatSpecUnderTolerance = %+.2w
  Inverted = false
  LineAngle = 0
  LockPosition = false
  MeasureType = 1
  OverTolerance = 0
  References2D = -> [SectionView]
  Rotation = 0
  Scale = 0.25
  ScaleType = 0
  TheoreticalExact = false
  Type = 1
  UnderTolerance = 0
  X = -2.05186
  Y = 47.7478
FEATURE [TechDraw::DrawViewDimension] Dimension017
  AngleOverride = false
  Arbitrary = false
  ArbitraryTolerances = false
  EqualTolerance = true
  ExtensionAngle = 0
  FormatSpec = %.2w
  FormatSpecOverTolerance = %+.2w
  FormatSpecUnderTolerance = %+.2w
  Inverted = false
  LineAngle = 0
  LockPosition = false
  MeasureType = 1
  OverTolerance = 0
  References2D = -> [ProjItem001]
  Rotation = 0
  Scale = 0.25
  ScaleType = 0
  TheoreticalExact = false
  Type = 2
  UnderTolerance = 0
  X = 12.694
  Y = 1.50769
FEATURE [TechDraw::DrawPage] Page001
  KeepUpdated = true
  NextBalloonIndex = 1
  ProjectionType = 0
  Scale = 0.25
  Template = -> Template001
  Views = -> [ProjGroup,Dimension001,SectionView,Dimension002,Dimension003,Dimension004,Dimension005,Dimension006,Annotation,Dimension007,Annotation003,Annotation004,Dimension016,Dimension017]
FEATURE [Part::Feature] Unfold
  shape: bbox 466.2 x 175.2 x 1.65 mm, 219 faces (baked)
FEATURE [TechDraw::DrawSVGTemplate] Template003
  EditableTexts = AUTHOR_NAME=P. Baus/J. Götzinger; DN=DN; DRAWING_TITLE=Backplane cover, unfolded; FC-DATE=07/01/2024; FC-REV=1.0.0; FC-SC=1:2; FC-SH=4 / 5; FC-SI=A4; FreeCAD_DRAWING=TUD, Institut für Angewandte Physik, APQ; PN=PN; SI-1=Email: <email>; SI-3=Material: Stainless steel 430
  Height = 210
  Orientation = 1
  Template = <path>
  Width = 297
FEATURE [Sketcher::SketchObject] Unfold_Sketch
  FullyConstrained = false
  sketch-geometry (217):
    g0: ArcOfCircle CenterX=-1.1781 CenterY=-24.9809 CenterZ=0 NormalX=0 NormalY=0 NormalZ=1 AngleXU=0 Radius=3 StartAngle=2.17659 EndAngle=2.5358
    g1: BSplineCurve PolesCount=15 KnotsCount=13 Degree=3 IsPeriodic=0
    g2: ArcOfCircle CenterX=-1.70824 CenterY=-24.9809 CenterZ=0 NormalX=0 NormalY=0 NormalZ=1 AngleXU=0 Radius=3 StartAngle=0.605792 EndAngle=0.965004
    g3: BSplineCurve PolesCount=15 KnotsCount=13 Degree=3 IsPeriodic=0
    g4: BSplineCurve PolesCount=15 KnotsCount=13 Degree=3 IsPeriodic=0
    g5: ArcOfCircle CenterX=-1.70824 CenterY=-24.4508 CenterZ=0 NormalX=0 NormalY=0 NormalZ=1 AngleXU=0 Radius=3 StartAngle=5.31818 EndAngle=5.67739
    g6: LineSegment StartX=3e-16 StartY=-26.9169 StartZ=0 EndX=3e-16 EndY=-47.159 EndZ=0
    g7: ArcOfCircle CenterX=1 CenterY=-47.159 CenterZ=0 NormalX=0 NormalY=0 NormalZ=1 AngleXU=-1.5708 Radius=1 StartAngle=4.71239 EndAngle=6.28319
    g8: LineSegment StartX=1 StartY=-48.159 StartZ=0 EndX=14.63 EndY=-48.159 EndZ=0
    g9: LineSegment StartX=14.63 StartY=-57.5454 StartZ=0 EndX=14.63 EndY=-48.159 EndZ=0
    g10: ArcOfCircle CenterX=15.63 CenterY=-57.5454 CenterZ=0 NormalX=0 NormalY=0 NormalZ=1 AngleXU=1.5708 Radius=1 StartAngle=1.5708 EndAngle=3.14159
    g11: LineSegment StartX=15.63 StartY=-58.5454 StartZ=0 EndX=54.27 EndY=-58.5454 EndZ=0
    g12: ArcOfCircle CenterX=54.27 CenterY=-57.5454 CenterZ=0 NormalX=0 NormalY=0 NormalZ=1 AngleXU=1.5708 Radius=1 StartAngle=3.14159 EndAngle=4.71239
    g13: LineSegment StartX=55.27 StartY=-57.5454 StartZ=0 EndX=55.27 EndY=-48.159 EndZ=0
    g14: LineSegment StartX=55.27 StartY=-48.159 StartZ=0 EndX=360.07 EndY=-48.159 EndZ=0
    g15: LineSegment StartX=360.07 StartY=-57.5454 StartZ=0 EndX=360.07 EndY=-48.159 EndZ=0
    g16: ArcOfCircle CenterX=361.07 CenterY=-57.5454 CenterZ=0 NormalX=0 NormalY=0 NormalZ=1 AngleXU=1.5708 Radius=1 StartAngle=1.5708 EndAngle=3.14159
    g17: LineSegment StartX=361.07 StartY=-58.5454 StartZ=0 EndX=399.71 EndY=-58.5454 EndZ=0
    g18: ArcOfCircle CenterX=399.71 CenterY=-57.5454 CenterZ=0 NormalX=0 NormalY=0 NormalZ=1 AngleXU=1.5708 Radius=1 StartAngle=3.14159 EndAngle=4.71239
    g19: LineSegment StartX=400.71 StartY=-57.5454 StartZ=0 EndX=400.71 EndY=-48.159 EndZ=0
    g20: LineSegment StartX=400.71 StartY=-48.159 StartZ=0 EndX=419.42 EndY=-48.159 EndZ=0
    g21: ArcOfCircle CenterX=419.42 CenterY=-47.159 CenterZ=0 NormalX=0 NormalY=0 NormalZ=1 AngleXU=-1.5708 Radius=1 StartAngle=0 EndAngle=1.5708
    g22: LineSegment StartX=420.42 StartY=-47.159 StartZ=0 EndX=420.42 EndY=-26.8162 EndZ=0
    g23: ArcOfCircle CenterX=422.187 CenterY=-24.3919 CenterZ=0 NormalX=0 NormalY=0 NormalZ=1 AngleXU=0 Radius=3 StartAngle=3.77147 EndAngle=4.08251
    g24: BSplineCurve PolesCount=15 KnotsCount=13 Degree=3 IsPeriodic=0
    g25: ArcOfCircle CenterX=422.187 CenterY=-25.0398 CenterZ=0 NormalX=0 NormalY=0 NormalZ=1 AngleXU=0 Radius=3 StartAngle=2.20068 EndAngle=2.51171
    g26: BSplineCurve PolesCount=15 KnotsCount=13 Degree=3 IsPeriodic=0
    g27: ArcOfCircle CenterX=421.539 CenterY=-25.0398 CenterZ=0 NormalX=0 NormalY=0 NormalZ=1 AngleXU=0 Radius=3 StartAngle=0.629881 EndAngle=0.940915
    g28: LineSegment StartX=423.963 StartY=-23.2727 StartZ=0 EndX=442.306 EndY=-23.2727 EndZ=0
    g29: ArcOfCircle CenterX=442.306 CenterY=-22.2727 CenterZ=0 NormalX=0 NormalY=0 NormalZ=1 AngleXU=-3.14159 Radius=1 StartAngle=1.5708 EndAngle=3.14159
    g30: LineSegment StartX=443.306 StartY=-22.2727 StartZ=0 EndX=443.306 EndY=80.4273 EndZ=0
    g31: ArcOfCircle CenterX=442.306 CenterY=80.4273 CenterZ=0 NormalX=0 NormalY=0 NormalZ=1 AngleXU=-3.14159 Radius=1 StartAngle=3.14159 EndAngle=4.71239
    g32: LineSegment StartX=442.306 StartY=81.4273 StartZ=0 EndX=423.963 EndY=81.4273 EndZ=0
    g33: ArcOfCircle CenterX=421.539 CenterY=83.1945 CenterZ=0 NormalX=0 NormalY=0 NormalZ=1 AngleXU=0 Radius=3 StartAngle=5.34227 EndAngle=5.6533
    g34: BSplineCurve PolesCount=15 KnotsCount=13 Degree=3 IsPeriodic=0
    g35: ArcOfCircle CenterX=422.187 CenterY=83.1945 CenterZ=0 NormalX=0 NormalY=0 NormalZ=1 AngleXU=0 Radius=3 StartAngle=3.77147 EndAngle=4.08251
    g36: BSplineCurve PolesCount=15 KnotsCount=13 Degree=3 IsPeriodic=0
    g37: ArcOfCircle CenterX=422.187 CenterY=82.5465 CenterZ=0 NormalX=0 NormalY=0 NormalZ=1 AngleXU=0 Radius=3 StartAngle=2.20068 EndAngle=2.51171
    g38: LineSegment StartX=420.42 StartY=105.314 StartZ=0 EndX=420.42 EndY=84.9708 EndZ=0
    g39: ArcOfCircle CenterX=419.42 CenterY=105.314 CenterZ=0 NormalX=0 NormalY=0 NormalZ=1 AngleXU=-1.5708 Radius=1 StartAngle=1.5708 EndAngle=3.14159
    g40: LineSegment StartX=400.71 StartY=106.314 StartZ=0 EndX=419.42 EndY=106.314 EndZ=0
    g41: LineSegment StartX=400.71 StartY=106.314 StartZ=0 EndX=400.71 EndY=115.7 EndZ=0
    g42: ArcOfCircle CenterX=399.71 CenterY=115.7 CenterZ=0 NormalX=0 NormalY=0 NormalZ=1 AngleXU=1.5708 Radius=1 StartAngle=4.71239 EndAngle=6.28319
    g43: LineSegment StartX=361.07 StartY=116.7 StartZ=0 EndX=399.71 EndY=116.7 EndZ=0
    g44: ArcOfCircle CenterX=361.07 CenterY=115.7 CenterZ=0 NormalX=0 NormalY=0 NormalZ=1 AngleXU=1.5708 Radius=1 StartAngle=0 EndAngle=1.5708
    g45: LineSegment StartX=360.07 StartY=106.314 StartZ=0 EndX=360.07 EndY=115.7 EndZ=0
    g46: LineSegment StartX=55.27 StartY=106.314 StartZ=0 EndX=360.07 EndY=106.314 EndZ=0
    g47: LineSegment StartX=55.27 StartY=106.314 StartZ=0 EndX=55.27 EndY=115.7 EndZ=0
    g48: ArcOfCircle CenterX=54.27 CenterY=115.7 CenterZ=0 NormalX=0 NormalY=0 NormalZ=1 AngleXU=1.5708 Radius=1 StartAngle=4.71239 EndAngle=6.28319
    g49: LineSegment StartX=15.63 StartY=116.7 StartZ=0 EndX=54.27 EndY=116.7 EndZ=0
    g50: ArcOfCircle CenterX=15.63 CenterY=115.7 CenterZ=0 NormalX=0 NormalY=0 NormalZ=1 AngleXU=1.5708 Radius=1 StartAngle=2.7e-15 EndAngle=1.5708
    g51: LineSegment StartX=14.63 StartY=106.314 StartZ=0 EndX=14.63 EndY=115.7 EndZ=0
    g52: LineSegment StartX=1 StartY=106.314 StartZ=0 EndX=14.63 EndY=106.314 EndZ=0
    g53: ArcOfCircle CenterX=1 CenterY=105.314 CenterZ=0 NormalX=0 NormalY=0 NormalZ=1 AngleXU=-1.5708 Radius=1 StartAngle=3.14159 EndAngle=4.71239
    g54: LineSegment StartX=0 StartY=85.0716 StartZ=0 EndX=0 EndY=105.314 EndZ=0
    g55: ArcOfCircle CenterX=-1.70824 CenterY=82.6054 CenterZ=0 NormalX=0 NormalY=0 NormalZ=1 AngleXU=0 Radius=3 StartAngle=0.605792 EndAngle=0.965004
    g56: BSplineCurve PolesCount=15 KnotsCount=13 Degree=3 IsPeriodic=0
    g57: BSplineCurve PolesCount=15 KnotsCount=13 Degree=3 IsPeriodic=0
    g58: ArcOfCircle CenterX=-1.70824 CenterY=83.1356 CenterZ=0 NormalX=0 NormalY=0 NormalZ=1 AngleXU=0 Radius=3 StartAngle=5.31818 EndAngle=5.67739
    g59: BSplineCurve PolesCount=15 KnotsCount=13 Degree=3 IsPeriodic=0
    g60: ArcOfCircle CenterX=-1.1781 CenterY=83.1356 CenterZ=0 NormalX=0 NormalY=0 NormalZ=1 AngleXU=0 Radius=3 StartAngle=3.74739 EndAngle=4.1066
    g61: LineSegment StartX=-21.8863 StartY=81.4273 StartZ=0 EndX=-3.64425 EndY=81.4273 EndZ=0
    g62: ArcOfCircle CenterX=-21.8863 CenterY=80.4273 CenterZ=0 NormalX=0 NormalY=0 NormalZ=1 AngleXU=-3.14159 Radius=1 StartAngle=4.71239 EndAngle=6.28319
    g63: LineSegment StartX=-22.8863 StartY=-22.2727 StartZ=0 EndX=-22.8863 EndY=80.4273 EndZ=0
    g64: ArcOfCircle CenterX=-21.8863 CenterY=-22.2727 CenterZ=0 NormalX=0 NormalY=0 NormalZ=1 AngleXU=-3.14159 Radius=1 StartAngle=0 EndAngle=1.5708
    g65: LineSegment StartX=-3.64425 StartY=-23.2727 StartZ=0 EndX=-21.8863 EndY=-23.2727 EndZ=0
    g66: Circle CenterX=45.11 CenterY=-37.159 CenterZ=0 NormalX=0 NormalY=0 NormalZ=-1 AngleXU=-3.14159 Radius=6.35
    g67: Circle CenterX=45.11 CenterY=-11.5627 CenterZ=0 NormalX=0 NormalY=0 NormalZ=-1 AngleXU=-3.14159 Radius=6.35
    g68: Circle CenterX=349.91 CenterY=69.7173 CenterZ=0 NormalX=0 NormalY=0 NormalZ=-1 AngleXU=-3.14159 Radius=5
    g69: Circle CenterX=268.63 CenterY=95.3137 CenterZ=0 NormalX=0 NormalY=0 NormalZ=1 AngleXU=0 Radius=5
    g70: Circle CenterX=207.67 CenterY=69.7173 CenterZ=0 NormalX=0 NormalY=0 NormalZ=-1 AngleXU=-3.14159 Radius=5
    g71: Circle CenterX=227.99 CenterY=69.7173 CenterZ=0 NormalX=0 NormalY=0 NormalZ=-1 AngleXU=-3.14159 Radius=5
    g72: Circle CenterX=248.31 CenterY=69.7173 CenterZ=0 NormalX=0 NormalY=0 NormalZ=-1 AngleXU=-3.14159 Radius=5
    g73: Circle CenterX=268.63 CenterY=69.7173 CenterZ=0 NormalX=0 NormalY=0 NormalZ=-1 AngleXU=-3.14159 Radius=5
    g74: Circle CenterX=288.95 CenterY=69.7173 CenterZ=0 NormalX=0 NormalY=0 NormalZ=-1 AngleXU=-3.14159 Radius=5
    g75: Circle CenterX=309.27 CenterY=69.7173 CenterZ=0 NormalX=0 NormalY=0 NormalZ=-1 AngleXU=-3.14159 Radius=5
    g76: Circle CenterX=329.59 CenterY=69.7173 CenterZ=0 NormalX=0 NormalY=0 NormalZ=-1 AngleXU=-3.14159 Radius=5
    g77: Circle CenterX=288.95 CenterY=95.3137 CenterZ=0 NormalX=0 NormalY=0 NormalZ=1 AngleXU=0 Radius=5
    g78: Circle CenterX=370.23 CenterY=69.7173 CenterZ=0 NormalX=0 NormalY=0 NormalZ=-1 AngleXU=-3.14159 Radius=5
    g79: Circle CenterX=390.55 CenterY=69.7173 CenterZ=0 NormalX=0 NormalY=0 NormalZ=-1 AngleXU=-3.14159 Radius=5
    g80: Circle CenterX=390.55 CenterY=95.3137 CenterZ=0 NormalX=0 NormalY=0 NormalZ=1 AngleXU=0 Radius=5
    g81: Circle CenterX=370.23 CenterY=95.3137 CenterZ=0 NormalX=0 NormalY=0 NormalZ=1 AngleXU=0 Radius=5
    g82: Circle CenterX=268.63 CenterY=29.0773 CenterZ=0 NormalX=0 NormalY=0 NormalZ=-1 AngleXU=-3.14159 Radius=5
    g83: Circle CenterX=349.91 CenterY=95.3137 CenterZ=0 NormalX=0 NormalY=0 NormalZ=1 AngleXU=0 Radius=5
    g84: Circle CenterX=329.59 CenterY=95.3137 CenterZ=0 NormalX=0 NormalY=0 NormalZ=1 AngleXU=0 Radius=5
    g85: Circle CenterX=309.27 CenterY=95.3137 CenterZ=0 NormalX=0 NormalY=0 NormalZ=1 AngleXU=0 Radius=5
    g86: Circle CenterX=329.59 CenterY=29.0773 CenterZ=0 NormalX=0 NormalY=0 NormalZ=-1 AngleXU=-3.14159 Radius=5
    g87: Circle CenterX=-13.8863 CenterY=-11.5627 CenterZ=0 NormalX=0 NormalY=0 NormalZ=-1 AngleXU=-1.5708 Radius=5
    g88: Circle CenterX=288.95 CenterY=29.0773 CenterZ=0 NormalX=0 NormalY=0 NormalZ=-1 AngleXU=-3.14159 Radius=5
    g89: Circle CenterX=207.67 CenterY=49.3973 CenterZ=0 NormalX=0 NormalY=0 NormalZ=-1 AngleXU=-3.14159 Radius=5
    g90: Circle CenterX=227.99 CenterY=49.3973 CenterZ=0 NormalX=0 NormalY=0 NormalZ=-1 AngleXU=-3.14159 Radius=5
    g91: Circle CenterX=248.31 CenterY=49.3973 CenterZ=0 NormalX=0 NormalY=0 NormalZ=-1 AngleXU=-3.14159 Radius=5
    g92: Circle CenterX=268.63 CenterY=49.3973 CenterZ=0 NormalX=0 NormalY=0 NormalZ=-1 AngleXU=-3.14159 Radius=5
    g93: Circle CenterX=288.95 CenterY=49.3973 CenterZ=0 NormalX=0 NormalY=0 NormalZ=-1 AngleXU=-3.14159 Radius=5
    g94: Circle CenterX=309.27 CenterY=29.0773 CenterZ=0 NormalX=0 NormalY=0 NormalZ=-1 AngleXU=-3.14159 Radius=5
    g95: Circle CenterX=390.55 CenterY=49.3973 CenterZ=0 NormalX=0 NormalY=0 NormalZ=-1 AngleXU=-3.14159 Radius=5
    g96: Circle CenterX=349.91 CenterY=29.0773 CenterZ=0 NormalX=0 NormalY=0 NormalZ=-1 AngleXU=-3.14159 Radius=5
    g97: Circle CenterX=370.23 CenterY=29.0773 CenterZ=0 NormalX=0 NormalY=0 NormalZ=-1 AngleXU=-3.14159 Radius=5
    g98: Circle CenterX=390.55 CenterY=29.0773 CenterZ=0 NormalX=0 NormalY=0 NormalZ=-1 AngleXU=-3.14159 Radius=5
    g99: Circle CenterX=309.27 CenterY=49.3973 CenterZ=0 NormalX=0 NormalY=0 NormalZ=-1 AngleXU=-3.14159 Radius=5
    g100: Circle CenterX=329.59 CenterY=49.3973 CenterZ=0 NormalX=0 NormalY=0 NormalZ=-1 AngleXU=-3.14159 Radius=5
    g101: Circle CenterX=349.91 CenterY=49.3973 CenterZ=0 NormalX=0 NormalY=0 NormalZ=-1 AngleXU=-3.14159 Radius=5
    g102: Circle CenterX=370.23 CenterY=49.3973 CenterZ=0 NormalX=0 NormalY=0 NormalZ=-1 AngleXU=-3.14159 Radius=5
    g103: Circle CenterX=227.99 CenterY=-37.159 CenterZ=0 NormalX=0 NormalY=0 NormalZ=-1 AngleXU=-3.14159 Radius=5
    g104: Circle CenterX=65.43 CenterY=-37.159 CenterZ=0 NormalX=0 NormalY=0 NormalZ=-1 AngleXU=-3.14159 Radius=5
    g105: Circle CenterX=85.75 CenterY=-37.159 CenterZ=0 NormalX=0 NormalY=0 NormalZ=-1 AngleXU=-3.14159 Radius=5
    g106: Circle CenterX=106.07 CenterY=-37.159 CenterZ=0 NormalX=0 NormalY=0 NormalZ=-1 AngleXU=-3.14159 Radius=5
    g107: Circle CenterX=126.39 CenterY=-37.159 CenterZ=0 NormalX=0 NormalY=0 NormalZ=-1 AngleXU=-3.14159 Radius=5
    g108: Circle CenterX=146.71 CenterY=-37.159 CenterZ=0 NormalX=0 NormalY=0 NormalZ=-1 AngleXU=-3.14159 Radius=5
    g109: Circle CenterX=167.03 CenterY=-37.159 CenterZ=0 NormalX=0 NormalY=0 NormalZ=-1 AngleXU=-3.14159 Radius=5
    g110: Circle CenterX=187.35 CenterY=-37.159 CenterZ=0 NormalX=0 NormalY=0 NormalZ=-1 AngleXU=-3.14159 Radius=5
    g111: Circle CenterX=207.67 CenterY=-37.159 CenterZ=0 NormalX=0 NormalY=0 NormalZ=-1 AngleXU=-3.14159 Radius=5
    g112: Circle CenterX=24.79 CenterY=-37.159 CenterZ=0 NormalX=0 NormalY=0 NormalZ=-1 AngleXU=-3.14159 Radius=5
    g113: Circle CenterX=248.31 CenterY=-37.159 CenterZ=0 NormalX=0 NormalY=0 NormalZ=-1 AngleXU=-3.14159 Radius=5
    g114: Circle CenterX=268.63 CenterY=-37.159 CenterZ=0 NormalX=0 NormalY=0 NormalZ=-1 AngleXU=-3.14159 Radius=5
    g115: Circle CenterX=288.95 CenterY=-37.159 CenterZ=0 NormalX=0 NormalY=0 NormalZ=-1 AngleXU=-3.14159 Radius=5
    g116: Circle CenterX=309.27 CenterY=-37.159 CenterZ=0 NormalX=0 NormalY=0 NormalZ=-1 AngleXU=-3.14159 Radius=5
    g117: Circle CenterX=329.59 CenterY=-37.159 CenterZ=0 NormalX=0 NormalY=0 NormalZ=-1 AngleXU=-3.14159 Radius=5
    g118: Circle CenterX=349.91 CenterY=-37.159 CenterZ=0 NormalX=0 NormalY=0 NormalZ=-1 AngleXU=-3.14159 Radius=5
    g119: Circle CenterX=370.23 CenterY=-37.159 CenterZ=0 NormalX=0 NormalY=0 NormalZ=-1 AngleXU=-3.14159 Radius=5
    g120: Circle CenterX=390.55 CenterY=-37.159 CenterZ=0 NormalX=0 NormalY=0 NormalZ=-1 AngleXU=-3.14159 Radius=5
    g121: Circle CenterX=65.43 CenterY=95.3137 CenterZ=0 NormalX=0 NormalY=0 NormalZ=1 AngleXU=0 Radius=5
    g122: Circle CenterX=227.99 CenterY=95.3137 CenterZ=0 NormalX=0 NormalY=0 NormalZ=1 AngleXU=0 Radius=5
    g123: Circle CenterX=207.67 CenterY=95.3137 CenterZ=0 NormalX=0 NormalY=0 NormalZ=1 AngleXU=0 Radius=5
    g124: Circle CenterX=187.35 CenterY=95.3137 CenterZ=0 NormalX=0 NormalY=0 NormalZ=1 AngleXU=0 Radius=5
    g125: Circle CenterX=167.03 CenterY=95.3137 CenterZ=0 NormalX=0 NormalY=0 NormalZ=1 AngleXU=0 Radius=5
    g126: Circle CenterX=146.71 CenterY=95.3137 CenterZ=0 NormalX=0 NormalY=0 NormalZ=1 AngleXU=0 Radius=5
    g127: Circle CenterX=126.39 CenterY=95.3137 CenterZ=0 NormalX=0 NormalY=0 NormalZ=1 AngleXU=0 Radius=5
    g128: Circle CenterX=106.07 CenterY=95.3137 CenterZ=0 NormalX=0 NormalY=0 NormalZ=1 AngleXU=0 Radius=5
    g129: Circle CenterX=85.75 CenterY=95.3137 CenterZ=0 NormalX=0 NormalY=0 NormalZ=1 AngleXU=0 Radius=5
    g130: Circle CenterX=248.31 CenterY=95.3137 CenterZ=0 NormalX=0 NormalY=0 NormalZ=1 AngleXU=0 Radius=5
    g131: Circle CenterX=45.11 CenterY=95.3137 CenterZ=0 NormalX=0 NormalY=0 NormalZ=1 AngleXU=0 Radius=5
    g132: Circle CenterX=24.79 CenterY=95.3137 CenterZ=0 NormalX=0 NormalY=0 NormalZ=1 AngleXU=0 Radius=5
    g133: Circle CenterX=434.306 CenterY=-11.5627 CenterZ=0 NormalX=0 NormalY=0 NormalZ=1 AngleXU=-1.5708 Radius=5
    g134: Circle CenterX=434.306 CenterY=8.75732 CenterZ=0 NormalX=0 NormalY=0 NormalZ=1 AngleXU=-1.5708 Radius=5
    g135: Circle CenterX=434.306 CenterY=29.0773 CenterZ=0 NormalX=0 NormalY=0 NormalZ=1 AngleXU=-1.5708 Radius=5
    g136: Circle CenterX=434.306 CenterY=49.3973 CenterZ=0 NormalX=0 NormalY=0 NormalZ=1 AngleXU=-1.5708 Radius=5
    g137: Circle CenterX=434.306 CenterY=69.7173 CenterZ=0 NormalX=0 NormalY=0 NormalZ=1 AngleXU=-1.5708 Radius=5
    g138: Circle CenterX=309.27 CenterY=-11.5627 CenterZ=0 NormalX=0 NormalY=0 NormalZ=-1 AngleXU=-3.14159 Radius=5
    g139: Circle CenterX=146.71 CenterY=8.75732 CenterZ=0 NormalX=0 NormalY=0 NormalZ=-1 AngleXU=-3.14159 Radius=5
    g140: Circle CenterX=167.03 CenterY=8.75732 CenterZ=0 NormalX=0 NormalY=0 NormalZ=-1 AngleXU=-3.14159 Radius=5
    g141: Circle CenterX=187.35 CenterY=8.75732 CenterZ=0 NormalX=0 NormalY=0 NormalZ=-1 AngleXU=-3.14159 Radius=5
    g142: Circle CenterX=207.67 CenterY=-11.5627 CenterZ=0 NormalX=0 NormalY=0 NormalZ=-1 AngleXU=-3.14159 Radius=5
    g143: Circle CenterX=227.99 CenterY=-11.5627 CenterZ=0 NormalX=0 NormalY=0 NormalZ=-1 AngleXU=-3.14159 Radius=5
    g144: Circle CenterX=248.31 CenterY=-11.5627 CenterZ=0 NormalX=0 NormalY=0 NormalZ=-1 AngleXU=-3.14159 Radius=5
    g145: Circle CenterX=268.63 CenterY=-11.5627 CenterZ=0 NormalX=0 NormalY=0 NormalZ=-1 AngleXU=-3.14159 Radius=5
    g146: Circle CenterX=288.95 CenterY=-11.5627 CenterZ=0 NormalX=0 NormalY=0 NormalZ=-1 AngleXU=-3.14159 Radius=5
    g147: Circle CenterX=126.39 CenterY=8.75732 CenterZ=0 NormalX=0 NormalY=0 NormalZ=-1 AngleXU=-3.14159 Radius=5
    g148: Circle CenterX=329.59 CenterY=-11.5627 CenterZ=0 NormalX=0 NormalY=0 NormalZ=-1 AngleXU=-3.14159 Radius=5
    g149: Circle CenterX=349.91 CenterY=-11.5627 CenterZ=0 NormalX=0 NormalY=0 NormalZ=-1 AngleXU=-3.14159 Radius=5
    g150: Circle CenterX=370.23 CenterY=-11.5627 CenterZ=0 NormalX=0 NormalY=0 NormalZ=-1 AngleXU=-3.14159 Radius=5
    g151: Circle CenterX=390.55 CenterY=-11.5627 CenterZ=0 NormalX=0 NormalY=0 NormalZ=-1 AngleXU=-3.14159 Radius=5
    g152: Circle CenterX=207.67 CenterY=8.75732 CenterZ=0 NormalX=0 NormalY=0 NormalZ=-1 AngleXU=-3.14159 Radius=5
    g153: Circle CenterX=227.99 CenterY=8.75732 CenterZ=0 NormalX=0 NormalY=0 NormalZ=-1 AngleXU=-3.14159 Radius=5
    g154: Circle CenterX=248.31 CenterY=8.75732 CenterZ=0 NormalX=0 NormalY=0 NormalZ=-1 AngleXU=-3.14159 Radius=5
    g155: Circle CenterX=268.63 CenterY=8.75732 CenterZ=0 NormalX=0 NormalY=0 NormalZ=-1 AngleXU=-3.14159 Radius=5
    g156: Circle CenterX=126.39 CenterY=-11.5627 CenterZ=0 NormalX=0 NormalY=0 NormalZ=-1 AngleXU=-3.14159 Radius=5
    g157: Circle CenterX=-13.8863 CenterY=8.75732 CenterZ=0 NormalX=0 NormalY=0 NormalZ=-1 AngleXU=-1.5708 Radius=5
    g158: Circle CenterX=-13.8863 CenterY=29.0773 CenterZ=0 NormalX=0 NormalY=0 NormalZ=-1 AngleXU=-1.5708 Radius=5
    g159: Circle CenterX=-13.8863 CenterY=49.3973 CenterZ=0 NormalX=0 NormalY=0 NormalZ=-1 AngleXU=-1.5708 Radius=5
    g160: Circle CenterX=-13.8863 CenterY=69.7173 CenterZ=0 NormalX=0 NormalY=0 NormalZ=-1 AngleXU=-1.5708 Radius=5
    g161: Circle CenterX=24.79 CenterY=-11.5627 CenterZ=0 NormalX=0 NormalY=0 NormalZ=-1 AngleXU=-3.14159 Radius=5
    g162: Circle CenterX=65.43 CenterY=-11.5627 CenterZ=0 NormalX=0 NormalY=0 NormalZ=-1 AngleXU=-3.14159 Radius=5
    g163: Circle CenterX=85.75 CenterY=-11.5627 CenterZ=0 NormalX=0 NormalY=0 NormalZ=-1 AngleXU=-3.14159 Radius=5
    g164: Circle CenterX=106.07 CenterY=-11.5627 CenterZ=0 NormalX=0 NormalY=0 NormalZ=-1 AngleXU=-3.14159 Radius=5
    g165: Circle CenterX=227.99 CenterY=29.0773 CenterZ=0 NormalX=0 NormalY=0 NormalZ=-1 AngleXU=-3.14159 Radius=5
    g166: Circle CenterX=146.71 CenterY=-11.5627 CenterZ=0 NormalX=0 NormalY=0 NormalZ=-1 AngleXU=-3.14159 Radius=5
    g167: Circle CenterX=167.03 CenterY=-11.5627 CenterZ=0 NormalX=0 NormalY=0 NormalZ=-1 AngleXU=-3.14159 Radius=5
    g168: Circle CenterX=187.35 CenterY=-11.5627 CenterZ=0 NormalX=0 NormalY=0 NormalZ=-1 AngleXU=-3.14159 Radius=5
    g169: Circle CenterX=24.79 CenterY=8.75732 CenterZ=0 NormalX=0 NormalY=0 NormalZ=-1 AngleXU=-3.14159 Radius=5
    g170: Circle CenterX=45.11 CenterY=8.75732 CenterZ=0 NormalX=0 NormalY=0 NormalZ=-1 AngleXU=-3.14159 Radius=5
    g171: Circle CenterX=65.43 CenterY=8.75732 CenterZ=0 NormalX=0 NormalY=0 NormalZ=-1 AngleXU=-3.14159 Radius=5
    g172: Circle CenterX=85.75 CenterY=8.75732 CenterZ=0 NormalX=0 NormalY=0 NormalZ=-1 AngleXU=-3.14159 Radius=5
    g173: Circle CenterX=106.07 CenterY=8.75732 CenterZ=0 NormalX=0 NormalY=0 NormalZ=-1 AngleXU=-3.14159 Radius=5
    g174: Circle CenterX=45.11 CenterY=69.7173 CenterZ=0 NormalX=0 NormalY=0 NormalZ=-1 AngleXU=-3.14159 Radius=5
    g175: Circle CenterX=126.39 CenterY=29.0773 CenterZ=0 NormalX=0 NormalY=0 NormalZ=-1 AngleXU=-3.14159 Radius=5
    g176: Circle CenterX=146.71 CenterY=29.0773 CenterZ=0 NormalX=0 NormalY=0 NormalZ=-1 AngleXU=-3.14159 Radius=5
    g177: Circle CenterX=167.03 CenterY=29.0773 CenterZ=0 NormalX=0 NormalY=0 NormalZ=-1 AngleXU=-3.14159 Radius=5
    g178: Circle CenterX=187.35 CenterY=29.0773 CenterZ=0 NormalX=0 NormalY=0 NormalZ=-1 AngleXU=-3.14159 Radius=5
    g179: Circle CenterX=126.39 CenterY=49.3973 CenterZ=0 NormalX=0 NormalY=0 NormalZ=-1 AngleXU=-3.14159 Radius=5
    g180: Circle CenterX=146.71 CenterY=49.3973 CenterZ=0 NormalX=0 NormalY=0 NormalZ=-1 AngleXU=-3.14159 Radius=5
    g181: Circle CenterX=167.03 CenterY=49.3973 CenterZ=0 NormalX=0 NormalY=0 NormalZ=-1 AngleXU=-3.14159 Radius=5
    g182: Circle CenterX=187.35 CenterY=49.3973 CenterZ=0 NormalX=0 NormalY=0 NormalZ=-1 AngleXU=-3.14159 Radius=5
    g183: Circle CenterX=24.79 CenterY=69.7173 CenterZ=0 NormalX=0 NormalY=0 NormalZ=-1 AngleXU=-3.14159 Radius=5
    g184: Circle CenterX=309.27 CenterY=8.75732 CenterZ=0 NormalX=0 NormalY=0 NormalZ=-1 AngleXU=-3.14159 Radius=5
    g185: Circle CenterX=65.43 CenterY=69.7173 CenterZ=0 NormalX=0 NormalY=0 NormalZ=-1 AngleXU=-3.14159 Radius=5
    g186: Circle CenterX=85.75 CenterY=69.7173 CenterZ=0 NormalX=0 NormalY=0 NormalZ=-1 AngleXU=-3.14159 Radius=5
    g187: Circle CenterX=106.07 CenterY=69.7173 CenterZ=0 NormalX=0 NormalY=0 NormalZ=-1 AngleXU=-3.14159 Radius=5
    g188: Circle CenterX=126.39 CenterY=69.7173 CenterZ=0 NormalX=0 NormalY=0 NormalZ=-1 AngleXU=-3.14159 Radius=5
    g189: Circle CenterX=146.71 CenterY=69.7173 CenterZ=0 NormalX=0 NormalY=0 NormalZ=-1 AngleXU=-3.14159 Radius=5
    g190: Circle CenterX=167.03 CenterY=69.7173 CenterZ=0 NormalX=0 NormalY=0 NormalZ=-1 AngleXU=-3.14159 Radius=5
    g191: Circle CenterX=187.35 CenterY=69.7173 CenterZ=0 NormalX=0 NormalY=0 NormalZ=-1 AngleXU=-3.14159 Radius=5
    g192: Circle CenterX=207.67 CenterY=29.0773 CenterZ=0 NormalX=0 NormalY=0 NormalZ=-1 AngleXU=-3.14159 Radius=5
    g193: Circle CenterX=248.31 CenterY=29.0773 CenterZ=0 NormalX=0 NormalY=0 NormalZ=-1 AngleXU=-3.14159 Radius=5
    g194: Circle CenterX=85.75 CenterY=49.3973 CenterZ=0 NormalX=0 NormalY=0 NormalZ=-1 AngleXU=-3.14159 Radius=5
    g195: Circle CenterX=288.95 CenterY=8.75732 CenterZ=0 NormalX=0 NormalY=0 NormalZ=-1 AngleXU=-3.14159 Radius=5
    g196: Circle CenterX=329.59 CenterY=8.75732 CenterZ=0 NormalX=0 NormalY=0 NormalZ=-1 AngleXU=-3.14159 Radius=5
    g197: Circle CenterX=349.91 CenterY=8.75732 CenterZ=0 NormalX=0 NormalY=0 NormalZ=-1 AngleXU=-3.14159 Radius=5
    g198: Circle CenterX=370.23 CenterY=8.75732 CenterZ=0 NormalX=0 NormalY=0 NormalZ=-1 AngleXU=-3.14159 Radius=5
    g199: Circle CenterX=390.55 CenterY=8.75732 CenterZ=0 NormalX=0 NormalY=0 NormalZ=-1 AngleXU=-3.14159 Radius=5
    g200: Circle CenterX=24.79 CenterY=29.0773 CenterZ=0 NormalX=0 NormalY=0 NormalZ=-1 AngleXU=-3.14159 Radius=5
    g201: Circle CenterX=45.11 CenterY=29.0773 CenterZ=0 NormalX=0 NormalY=0 NormalZ=-1 AngleXU=-3.14159 Radius=5
    g202: Circle CenterX=65.43 CenterY=29.0773 CenterZ=0 NormalX=0 NormalY=0 NormalZ=-1 AngleXU=-3.14159 Radius=5
    g203: Circle CenterX=85.75 CenterY=29.0773 CenterZ=0 NormalX=0 NormalY=0 NormalZ=-1 AngleXU=-3.14159 Radius=5
    g204: Circle CenterX=106.07 CenterY=29.0773 CenterZ=0 NormalX=0 NormalY=0 NormalZ=-1 AngleXU=-3.14159 Radius=5
    g205: Circle CenterX=24.79 CenterY=49.3973 CenterZ=0 NormalX=0 NormalY=0 NormalZ=-1 AngleXU=-3.14159 Radius=5
    g206: Circle CenterX=45.11 CenterY=49.3973 CenterZ=0 NormalX=0 NormalY=0 NormalZ=-1 AngleXU=-3.14159 Radius=5
    g207: Circle CenterX=65.43 CenterY=49.3973 CenterZ=0 NormalX=0 NormalY=0 NormalZ=-1 AngleXU=-3.14159 Radius=5
    g208: Circle CenterX=106.07 CenterY=49.3973 CenterZ=0 NormalX=0 NormalY=0 NormalZ=-1 AngleXU=-3.14159 Radius=5
    g209: LineSegment StartX=-1.44317 StartY=-21.9809 StartZ=0 EndX=-1.44317 EndY=80.1356 EndZ=0
    g210: LineSegment StartX=421.863 StartY=-22.0398 StartZ=0 EndX=421.863 EndY=80.1945 EndZ=0
    g211: LineSegment StartX=360.07 StartY=-49.6022 StartZ=0 EndX=400.71 EndY=-49.6022 EndZ=0
    g212: LineSegment StartX=14.63 StartY=-49.6022 StartZ=0 EndX=55.27 EndY=-49.6022 EndZ=0
    g213: LineSegment StartX=1.29176 StartY=-24.7158 StartZ=0 EndX=419.187 EndY=-24.7158 EndZ=0
    g214: LineSegment StartX=1.29176 StartY=82.8705 StartZ=0 EndX=419.187 EndY=82.8705 EndZ=0
    g215: LineSegment StartX=14.63 StartY=107.757 StartZ=0 EndX=55.27 EndY=107.757 EndZ=0
    g216: LineSegment StartX=360.07 StartY=107.757 StartZ=0 EndX=400.71 EndY=107.757 EndZ=0
FEATURE [TechDraw::DrawViewPart] View002
  CoarseView = false
  Direction = (0,0,-1)
  Focus = 100
  HardHidden = false
  IsoCount = 0
  IsoHidden = false
  IsoVisible = false
  LockPosition = false
  Perspective = false
  Rotation = 0
  Scale = 0.5
  ScaleType = 0
  ScrubCount = 0
  SeamHidden = false
  SeamVisible = true
  SmoothHidden = false
  SmoothVisible = true
  Source = -> [Unfold_Sketch]
  X = 166.122
  XDirection = (1,0,0)
  Y = 126.16
FEATURE [TechDraw::DrawViewAnnotation] Annotation005
  Font = osifont
  LineSpace = 100
  LockPosition = false
  MaxWidth = -1
  Rotation = 0
  Scale = 0.5
  ScaleType = 0
  Text = Unfolded using a k-factor of 0.45, assuming stainless steel 430 and a sheet thickness of 1.5 mm. | This drawing is for reference only and a different process may require a different unfolding procedure.
  TextSize = 2.5
  TextStyle = 0
  X = 85.5724
  Y = 182.886
FEATURE [TechDraw::DrawViewDimension] Dimension018
  AngleOverride = false
  Arbitrary = false
  ArbitraryTolerances = false
  EqualTolerance = true
  ExtensionAngle = 0
  FormatSpec = %.2w
  FormatSpecOverTolerance = %+.2w
  FormatSpecUnderTolerance = %+.2w
  Inverted = false
  LineAngle = 0
  LockPosition = false
  MeasureType = 1
  OverTolerance = 0
  References2D = -> [View002]
  Rotation = 0
  Scale = 0.5
  ScaleType = 0
  TheoreticalExact = false
  Type = 2
  UnderTolerance = 0
  X = -151.72
  Y = 0
FEATURE [TechDraw::DrawViewDimension] Dimension019
  AngleOverride = false
  Arbitrary = false
  ArbitraryTolerances = false
  EqualTolerance = true
  ExtensionAngle = 0
  FormatSpec = %.2w
  FormatSpecOverTolerance = %+.2w
  FormatSpecUnderTolerance = %+.2w
  Inverted = false
  LineAngle = 0
  LockPosition = false
  MeasureType = 1
  OverTolerance = 0
  References2D = -> [View002]
  Rotation = 0
  Scale = 0.5
  ScaleType = 0
  TheoreticalExact = false
  Type = 2
  UnderTolerance = 0
  X = -145.529
  Y = 0
FEATURE [TechDraw::DrawViewDimension] Dimension020
  AngleOverride = false
  Arbitrary = false
  ArbitraryTolerances = false
  EqualTolerance = true
  ExtensionAngle = 0
  FormatSpec = %.2w
  FormatSpecOverTolerance = %+.2w
  FormatSpecUnderTolerance = %+.2w
  Inverted = false
  LineAngle = 0
  LockPosition = false
  MeasureType = 1
  OverTolerance = 0
  References2D = -> [View002]
  Rotation = 0
  Scale = 0.5
  ScaleType = 0
  TheoreticalExact = false
  Type = 2
  UnderTolerance = 0
  X = -140.423
  Y = 0
FEATURE [TechDraw::DrawViewDimension] Dimension021
  AngleOverride = false
  Arbitrary = false
  ArbitraryTolerances = false
  EqualTolerance = true
  ExtensionAngle = 0
  FormatSpec = %.2w
  FormatSpecOverTolerance = %+.2w
  FormatSpecUnderTolerance = %+.2w
  Inverted = false
  LineAngle = 0
  LockPosition = false
  MeasureType = 1
  OverTolerance = 0
  References2D = -> [View002]
  Rotation = 0
  Scale = 0.5
  ScaleType = 0
  TheoreticalExact = false
  Type = 2
  UnderTolerance = 0
  X = -134.666
  Y = 0
FEATURE [TechDraw::DrawViewDimension] Dimension022
  AngleOverride = false
  Arbitrary = false
  ArbitraryTolerances = false
  EqualTolerance = true
  ExtensionAngle = 0
  FormatSpec = %.2w
  FormatSpecOverTolerance = %+.2w
  FormatSpecUnderTolerance = %+.2w
  Inverted = false
  LineAngle = 0
  LockPosition = false
  MeasureType = 1
  OverTolerance = 0
  References2D = -> [View002]
  Rotation = 0
  Scale = 0.5
  ScaleType = 0
  TheoreticalExact = false
  Type = 2
  UnderTolerance = 0
  X = -127.324
  Y = 0
FEATURE [TechDraw::DrawViewDimension] Dimension023
  AngleOverride = false
  Arbitrary = false
  ArbitraryTolerances = false
  EqualTolerance = true
  ExtensionAngle = 0
  FormatSpec = %.2w
  FormatSpecOverTolerance = %+.2w
  FormatSpecUnderTolerance = %+.2w
  Inverted = false
  LineAngle = 0
  LockPosition = false
  MeasureType = 1
  OverTolerance = 0
  References2D = -> [View002]
  Rotation = 0
  Scale = 0.5
  ScaleType = 0
  TheoreticalExact = false
  Type = 1
  UnderTolerance = 0
  X = 0
  Y = -70.905
FEATURE [TechDraw::DrawViewDimension] Dimension024
  AngleOverride = false
  Arbitrary = false
  ArbitraryTolerances = false
  EqualTolerance = true
  ExtensionAngle = 0
  FormatSpec = %.2w
  FormatSpecOverTolerance = %+.2w
  FormatSpecUnderTolerance = %+.2w
  Inverted = false
  LineAngle = 0
  LockPosition = false
  MeasureType = 1
  OverTolerance = 0
  References2D = -> [View002]
  Rotation = 0
  Scale = 0.5
  ScaleType = 0
  TheoreticalExact = false
  Type = 1
  UnderTolerance = 0
  X = 0
  Y = -65.905
FEATURE [TechDraw::DrawViewDimension] Dimension025
  AngleOverride = false
  Arbitrary = false
  ArbitraryTolerances = false
  EqualTolerance = true
  ExtensionAngle = 0
  FormatSpec = %.2w
  FormatSpecOverTolerance = %+.2w
  FormatSpecUnderTolerance = %+.2w
  Inverted = false
  LineAngle = 0
  LockPosition = false
  MeasureType = 1
  OverTolerance = 0
  References2D = -> [View002]
  Rotation = 0
  Scale = 0.5
  ScaleType = 0
  TheoreticalExact = false
  Type = 1
  UnderTolerance = 0
  X = 0
  Y = -60.905
FEATURE [TechDraw::DrawViewDimension] Dimension026
  AngleOverride = false
  Arbitrary = false
  ArbitraryTolerances = false
  EqualTolerance = true
  ExtensionAngle = 0
  FormatSpec = %.2w
  FormatSpecOverTolerance = %+.2w
  FormatSpecUnderTolerance = %+.2w
  Inverted = false
  LineAngle = 0
  LockPosition = false
  MeasureType = 1
  OverTolerance = 0
  References2D = -> [View002]
  Rotation = 0
  Scale = 0.5
  ScaleType = 0
  TheoreticalExact = false
  Type = 1
  UnderTolerance = 0
  X = 0
  Y = -55.481
FEATURE [TechDraw::DrawViewDimension] Dimension027
  AngleOverride = false
  Arbitrary = false
  ArbitraryTolerances = false
  EqualTolerance = true
  ExtensionAngle = 0
  FormatSpec = %.2w
  FormatSpecOverTolerance = %+.2w
  FormatSpecUnderTolerance = %+.2w
  Inverted = false
  LineAngle = 0
  LockPosition = false
  MeasureType = 1
  OverTolerance = 0
  References2D = -> [View002]
  Rotation = 0
  Scale = 0.5
  ScaleType = 0
  TheoreticalExact = false
  Type = 1
  UnderTolerance = 0
  X = 0
  Y = -50.481
FEATURE [TechDraw::DrawPage] Page003
  KeepUpdated = true
  NextBalloonIndex = 1
  ProjectionType = 0
  Scale = 0.5
  Template = -> Template003
  Views = -> [View002,Annotation005,Dimension018,Dimension019,Dimension020,Dimension021,Dimension022,Dimension023,Dimension024,Dimension025,Dimension026,Dimension027]
FEATURE [TechDraw::DrawSVGTemplate] Template004
  EditableTexts = AUTHOR_NAME=P. Baus/J. Götzinger; DN=DN; DRAWING_TITLE=Backplane cover, unfolded; FC-DATE=07/01/2024; FC-REV=1.0.0; FC-SC=1:2; FC-SH=5 / 5; FC-SI=A4; FreeCAD_DRAWING=TUD, Institut für Angewandte Physik, APQ; PN=PN; SI-1=Email: <email>; SI-3=Material: Stainless steel 430
  Height = 210
  Orientation = 1
  Template = <path>
  Width = 297
FEATURE [TechDraw::DrawViewPart] View003
  CoarseView = false
  Direction = (0,0,1)
  Focus = 100
  HardHidden = false
  IsoCount = 0
  IsoHidden = false
  IsoVisible = false
  LockPosition = false
  Perspective = false
  Rotation = 0
  Scale = 0.5
  ScaleType = 0
  ScrubCount = 0
  SeamHidden = false
  SeamVisible = true
  SmoothHidden = false
  SmoothVisible = true
  Source = -> [Unfold_Sketch]
  X = 162.781
  XDirection = (1,0,0)
  Y = 129.7
FEATURE [TechDraw::DrawViewDimension] Dimension028
  AngleOverride = false
  Arbitrary = false
  ArbitraryTolerances = false
  EqualTolerance = true
  ExtensionAngle = 0
  FormatSpec = %.2w
  FormatSpecOverTolerance = %+.2w
  FormatSpecUnderTolerance = %+.2w
  Inverted = false
  LineAngle = 0
  LockPosition = false
  MeasureType = 1
  OverTolerance = 0
  References2D = -> [View003]
  Rotation = 0
  Scale = 0.5
  ScaleType = 0
  TheoreticalExact = false
  Type = 2
  UnderTolerance = 0
  X = -129.02
  Y = -37.2148
FEATURE [TechDraw::DrawViewDimension] Dimension029
  AngleOverride = false
  Arbitrary = false
  ArbitraryTolerances = false
  EqualTolerance = true
  ExtensionAngle = 0
  FormatSpec = %.2w
  FormatSpecOverTolerance = %+.2w
  FormatSpecUnderTolerance = %+.2w
  Inverted = false
  LineAngle = 0
  LockPosition = false
  MeasureType = 1
  OverTolerance = 0
  References2D = -> [View003]
  Rotation = 0
  Scale = 0.5
  ScaleType = 0
  TheoreticalExact = false
  Type = 2
  UnderTolerance = 0
  X = -136.02
  Y = -30.8157
FEATURE [TechDraw::DrawViewDimension] Dimension031
  AngleOverride = false
  Arbitrary = false
  ArbitraryTolerances = false
  EqualTolerance = true
  ExtensionAngle = 0
  FormatSpec = %.2w
  FormatSpecOverTolerance = %+.2w
  FormatSpecUnderTolerance = %+.2w
  Inverted = false
  LineAngle = 0
  LockPosition = false
  MeasureType = 1
  OverTolerance = 0
  References2D = -> [View003]
  Rotation = 0
  Scale = 0.5
  ScaleType = 0
  TheoreticalExact = false
  Type = 2
  UnderTolerance = 0
  X = -136.02
  Y = -13.99
FEATURE [TechDraw::DrawViewDimension] Dimension032
  AngleOverride = false
  Arbitrary = false
  ArbitraryTolerances = false
  EqualTolerance = true
  ExtensionAngle = 0
  FormatSpec = %.2w
  FormatSpecOverTolerance = %+.2w
  FormatSpecUnderTolerance = %+.2w
  Inverted = false
  LineAngle = 0
  LockPosition = false
  MeasureType = 1
  OverTolerance = 0
  References2D = -> [View003]
  Rotation = 0
  Scale = 0.5
  ScaleType = 0
  TheoreticalExact = false
  Type = 1
  UnderTolerance = 0
  X = -124.651
  Y = -54.5989
FEATURE [TechDraw::DrawViewDimension] Dimension033
  AngleOverride = false
  Arbitrary = false
  ArbitraryTolerances = false
  EqualTolerance = true
  ExtensionAngle = 0
  FormatSpec = %.2w
  FormatSpecOverTolerance = %+.2w
  FormatSpecUnderTolerance = %+.2w
  Inverted = false
  LineAngle = 0
  LockPosition = false
  MeasureType = 1
  OverTolerance = 0
  References2D = -> [View003]
  Rotation = 0
  Scale = 0.5
  ScaleType = 0
  TheoreticalExact = false
  Type = 1
  UnderTolerance = 0
  X = -104.629
  Y = -61.3657
FEATURE [TechDraw::DrawViewDimension] Dimension034
  AngleOverride = false
  Arbitrary = false
  ArbitraryTolerances = false
  EqualTolerance = true
  ExtensionAngle = 0
  FormatSpec = %.2w
  FormatSpecOverTolerance = %+.2w
  FormatSpecUnderTolerance = %+.2w
  Inverted = false
  LineAngle = 0
  LockPosition = false
  MeasureType = 1
  OverTolerance = 0
  References2D = -> [View003]
  Rotation = 0
  Scale = 0.5
  ScaleType = 0
  TheoreticalExact = false
  Type = 1
  UnderTolerance = 0
  X = -87.63
  Y = -61.366
FEATURE [TechDraw::DrawViewBalloon] Balloon001
  BubbleShape = 7
  EndType = 0
  EndTypeScale = 1
  KinkLength = 5
  LockPosition = false
  OriginX = 0.0294524
  OriginY = 53.7932
  Rotation = 0
  Scale = 0.5
  ScaleType = 0
  ShapeScale = 1
  SourceView = -> View003
  Text = UP 90° R1.5
  TextWrapLen = -1
  X = -49.0214
  Y = 103.483
FEATURE [TechDraw::DrawViewBalloon] Balloon002
  BubbleShape = 7
  EndType = 0
  EndTypeScale = 1
  KinkLength = 5
  LockPosition = false
  OriginX = -211.653
  OriginY = 4.55e-14
  Rotation = 0
  Scale = 0.5
  ScaleType = 0
  ShapeScale = 1
  SourceView = -> View003
  Text = UP 90° R1.5
  TextWrapLen = -1
  X = -263.934
  Y = 61.2246
FEATURE [TechDraw::DrawViewBalloon] Balloon003
  BubbleShape = 7
  EndType = 0
  EndTypeScale = 1
  KinkLength = 5
  LockPosition = false
  OriginX = 0.0294524
  OriginY = -53.7932
  Rotation = 0
  Scale = 0.5
  ScaleType = 0
  ShapeScale = 1
  SourceView = -> View003
  Text = UP 90° R1.5
  TextWrapLen = -1
  X = -67.4776
  Y = -113.456
FEATURE [TechDraw::DrawViewBalloon] Balloon004
  BubbleShape = 7
  EndType = 0
  EndTypeScale = 1
  KinkLength = 5
  LockPosition = false
  OriginX = 211.653
  OriginY = 4.55e-14
  Rotation = 0
  Scale = 0.5
  ScaleType = 0
  ShapeScale = 1
  SourceView = -> View003
  Text = UP 90° R1.5
  TextWrapLen = -1
  X = 208.743
  Y = -113.186
FEATURE [TechDraw::DrawViewBalloon] Balloon005
  BubbleShape = 7
  EndType = 0
  EndTypeScale = 1
  KinkLength = 5
  LockPosition = false
  OriginX = -175.26
  OriginY = 78.6795
  Rotation = 0
  Scale = 0.5
  ScaleType = 0
  ShapeScale = 1
  SourceView = -> View003
  Text = DOWN 90° R1.5
  TextWrapLen = -1
  X = -213.237
  Y = 108.529
FEATURE [TechDraw::DrawViewBalloon] Balloon006
  BubbleShape = 7
  EndType = 0
  EndTypeScale = 1
  KinkLength = 5
  LockPosition = false
  OriginX = 170.18
  OriginY = 78.6795
  Rotation = 0
  Scale = 0.5
  ScaleType = 0
  ShapeScale = 1
  SourceView = -> View003
  Text = DOWN 90° R1.5
  TextWrapLen = -1
  X = 129.434
  Y = 108.99
FEATURE [TechDraw::DrawViewBalloon] Balloon007
  BubbleShape = 7
  EndType = 0
  EndTypeScale = 1
  KinkLength = 5
  LockPosition = false
  OriginX = -175.26
  OriginY = -78.6795
  Rotation = 0
  Scale = 0.5
  ScaleType = 0
  ShapeScale = 1
  SourceView = -> View003
  Text = DOWN 90° R1.5
  TextWrapLen = -1
  X = -128.8
  Y = -120.809
FEATURE [TechDraw::DrawViewBalloon] Balloon008
  BubbleShape = 7
  EndType = 0
  EndTypeScale = 1
  KinkLength = 5
  LockPosition = false
  OriginX = 170.18
  OriginY = -78.6795
  Rotation = 0
  Scale = 0.5
  ScaleType = 0
  ShapeScale = 1
  SourceView = -> View003
  Text = DOWN 90° R1.5
  TextWrapLen = -1
  X = 106.826
  Y = -120.809
FEATURE [TechDraw::DrawPage] Page004
  KeepUpdated = true
  NextBalloonIndex = 11
  ProjectionType = 0
  Scale = 0.5
  Template = -> Template004
  Views = -> [View003,Dimension028,Dimension029,Dimension031,Dimension032,Dimension033,Dimension034,Balloon001,Balloon002,Balloon003,Balloon004,Balloon005,Balloon006,Balloon007,Balloon008]
note: 7 file-system paths scrubbed to <path> (originals preserved in the JSON sidecar)
